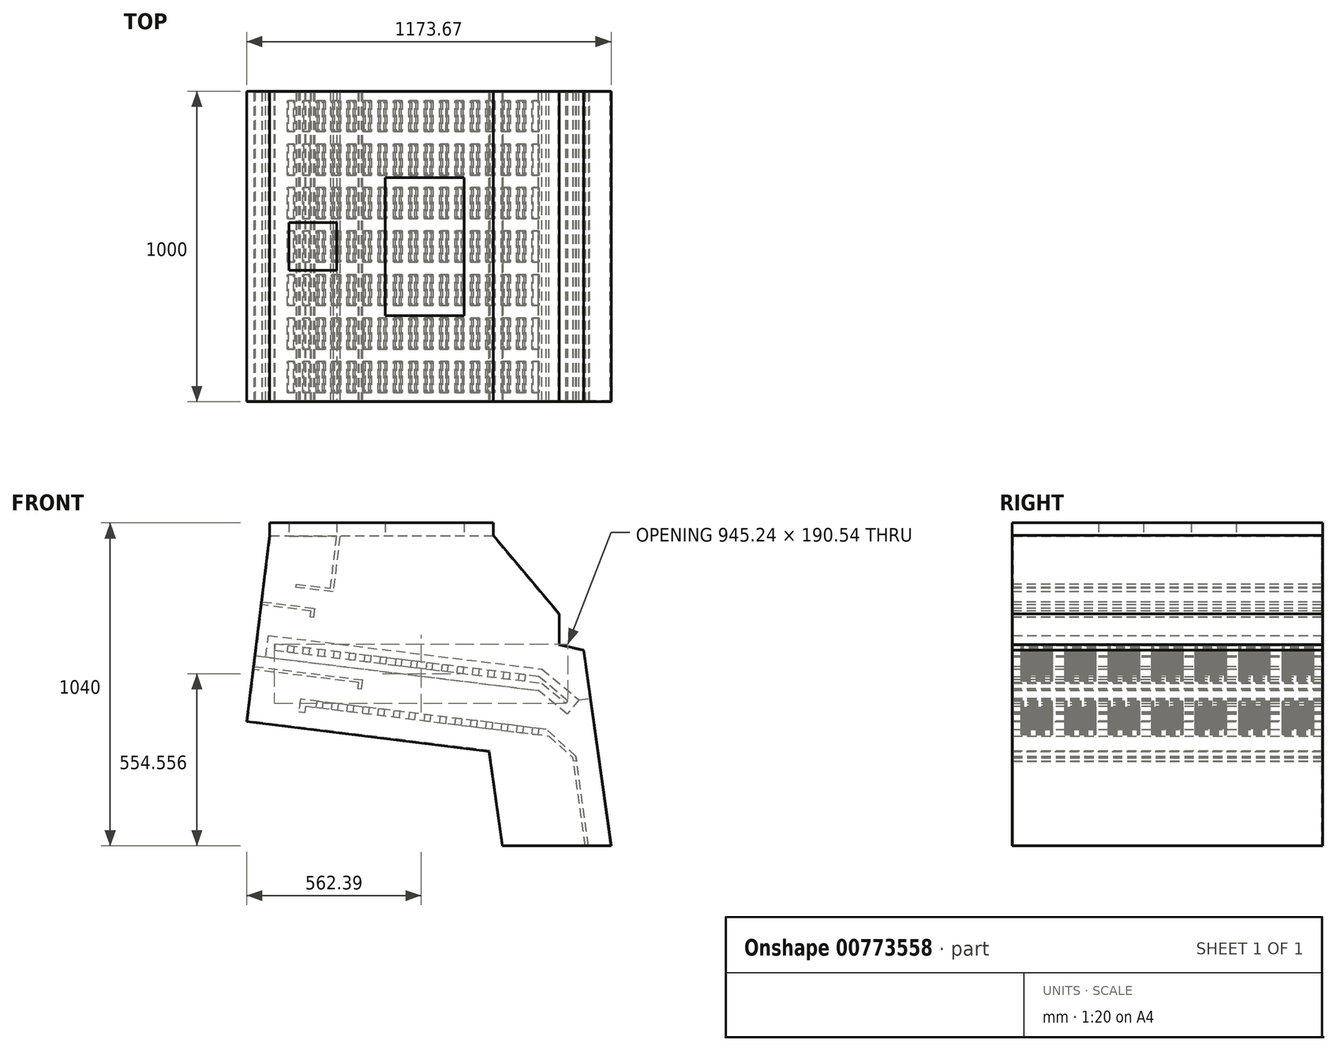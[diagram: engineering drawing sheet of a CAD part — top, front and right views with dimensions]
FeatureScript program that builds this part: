
annotation { "Feature Type Name" : "Feature", "Feature Type Description" : "" }
export const myFeature = defineFeature(function(context is Context, id is Id, definition is map)
    precondition{}
    {
        {
            var Q0;
            Q0=qCreatedBy(makeId("Front.planeOp"),FACE);
            var sketch = newSketch(context, id + "F0", { "sketchPlane" : qUnion([Q0])});
            skLineSegment(sketch, "E0.bottom", {"start": v(-500, 500) * mm, "end": v(600, 500) * mm, "construction": true});
            skLineSegment(sketch, "E0.top", {"start": v(-500, -500) * mm, "end": v(600, -500) * mm, "construction": true});
            skLineSegment(sketch, "E0.left", {"start": v(-500, 500) * mm, "end": v(-500, -500) * mm, "construction": true});
            skLineSegment(sketch, "E0.right", {"start": v(600, 500) * mm, "end": v(600, -500) * mm, "construction": true});
            skLineSegment(sketch, "E1", {"start": v(250, -500) * mm, "end": v(207.26, -195.89) * mm});
            skLineSegment(sketch, "E2", {"start": v(207.26, -195.89) * mm, "end": v(-573.67, -100) * mm});
            skLineSegment(sketch, "E3", {"start": v(433.06, 247.65) * mm, "end": v(221.32, 500) * mm});
            skLineSegment(sketch, "E4", {"start": v(221.32, 500) * mm, "end": v(-500, 500) * mm});
            skLineSegment(sketch, "E5", {"start": v(-500, 500) * mm, "end": v(-573.67, -100) * mm});
            skLineSegment(sketch, "E6", {"start": v(433.06, 247.65) * mm, "end": v(433.06, 147.65) * mm});
            skLineSegment(sketch, "E7", {"start": v(433.06, 147.65) * mm, "end": v(511.32, 131.02) * mm});
            skLineSegment(sketch, "E8", {"start": v(511.32, 131.02) * mm, "end": v(600, -500) * mm});
            skLineSegment(sketch, "E9", {"start": v(600, -500) * mm, "end": v(250, -500) * mm});
            skLineSegment(sketch, "E10", {"start": v(-573.67, -100) * mm, "end": v(788.77, -267.29) * mm, "construction": true});
            skSolve(sketch);
        }
        {
            var Q0;
            Q0 = qSketchRegion(id + "F0", true);
            extrude(context, id + "F1", {"entities" : qUnion([Q0]), "endBound" : BoundingType.SYMMETRIC, "depth" : 1000 * mm, "offsetDistance" : 25 * mm, "hasSecondDirection" : true, "secondDirectionOppositeDirection" : true, "secondDirectionDepth" : 500 * mm});
        }
        {
            var Q0;
            Q0=makeQuery(id+"F1.opExtrude","SWEPT_FACE",FACE,{"disambiguationData":[OSD([sQuery(id+"F0.wireOp",EDGE,"E4")])]});
            var sketch = newSketch(context, id + "F2", { "sketchPlane" : qUnion([Q0])});
            skLineSegment(sketch, "E11.bottom", {"start": v(-440, 80) * mm, "end": v(-280, 80) * mm});
            skLineSegment(sketch, "E11.top", {"start": v(-440, -80) * mm, "end": v(-280, -80) * mm});
            skLineSegment(sketch, "E11.left", {"start": v(-440, 80) * mm, "end": v(-440, -80) * mm});
            skLineSegment(sketch, "E11.right", {"start": v(-280, 80) * mm, "end": v(-280, -80) * mm});
            skSolve(sketch);
        }
        {
            var Q0;
            Q0 = qSketchRegion(id + "F2", true);
            extrude(context, id + "F3", {"entities" : qUnion([Q0]), "operationType" : NewBodyOperationType.ADD, "depth" : 40 * mm, "offsetDistance" : 25 * mm});
        }
        {
            var Q0;
            Q0=makeQuery(id+"F1.opExtrude","SWEPT_FACE",FACE,{"disambiguationData":[OSD([sQuery(id+"F0.wireOp",EDGE,"E4")])]});
            var sketch = newSketch(context, id + "F4", { "sketchPlane" : qUnion([Q0])});
            skLineSegment(sketch, "E12.bottom", {"start": v(130, 225) * mm, "end": v(-130, 225) * mm});
            skLineSegment(sketch, "E12.top", {"start": v(130, -225) * mm, "end": v(-130, -225) * mm});
            skLineSegment(sketch, "E12.left", {"start": v(130, 225) * mm, "end": v(130, -225) * mm});
            skLineSegment(sketch, "E12.right", {"start": v(-130, 225) * mm, "end": v(-130, -225) * mm});
            skSolve(sketch);
        }
        {
            var Q0;
            Q0 = qSketchRegion(id + "F4", true);
            extrude(context, id + "F5", {"entities" : qUnion([Q0]), "operationType" : NewBodyOperationType.ADD, "depth" : 40 * mm, "offsetDistance" : 25 * mm});
        }
        {
            var Q0;
            Q0=makeQuery(id+"F3.opExtrude","CAP_FACE",FACE,{"disambiguationData":[OSD([sQuery(id+"F2.wireOp",EDGE,"E11.bottom"),sQuery(id+"F2.wireOp",EDGE,"E11.top"),sQuery(id+"F2.wireOp",EDGE,"E11.left"),sQuery(id+"F2.wireOp",EDGE,"E11.right")])],"isStart":false});
            var Q1;
            Q1=makeQuery(id+"F5.opExtrude","CAP_FACE",FACE,{"disambiguationData":[OSD([sQuery(id+"F4.wireOp",EDGE,"E12.bottom"),sQuery(id+"F4.wireOp",EDGE,"E12.top"),sQuery(id+"F4.wireOp",EDGE,"E12.left"),sQuery(id+"F4.wireOp",EDGE,"E12.right")])],"isStart":false});
            var Q2;
            Q2=makeQuery(id+"F1.opExtrude","SWEPT_FACE",FACE,{"disambiguationData":[OSD([sQuery(id+"F0.wireOp",EDGE,"EKClBvXg-2bRz-m1K9-gZvp-cbB6sfYIkZG2")])]});
            var Q3;
            Q3=makeQuery(id+"F1.opExtrude","SWEPT_FACE",FACE,{"disambiguationData":[OSD([sQuery(id+"F0.wireOp",EDGE,"E9")])]});
            var Q4;
            Q4=makeQuery(id+"F1.opExtrude","SWEPT_BODY",BODY,{"disambiguationData":[OSD([sQuery(id+"F0.wireOp",EDGE,"E1"),sQuery(id+"F0.wireOp",EDGE,"E2"),sQuery(id+"F0.wireOp",EDGE,"E3"),sQuery(id+"F0.wireOp",EDGE,"E4"),sQuery(id+"F0.wireOp",EDGE,"E5"),sQuery(id+"F0.wireOp",EDGE,"E6"),sQuery(id+"F0.wireOp",EDGE,"E7"),sQuery(id+"F0.wireOp",EDGE,"E8"),sQuery(id+"F0.wireOp",EDGE,"xE1LlFz5-4HxX-VpLr-CkL3-rUP58BRSOtdD"),sQuery(id+"F0.wireOp",EDGE,"ObRK8uaC-pM7K-56M3-T9gG-oIo7mZDbm86T"),sQuery(id+"F0.wireOp",EDGE,"EFww76GN-BGT8-24En-PaDw-SS0GAKKsnwer"),sQuery(id+"F0.wireOp",EDGE,"E9"),sQuery(id+"F0.wireOp",EDGE,"EKClBvXg-2bRz-m1K9-gZvp-cbB6sfYIkZG2")])]});
            shell(context, id + "F6", {"entities" : qUnion([Q0, Q1, Q2, Q3]), "parts" : qUnion([Q4]), "thickness" : 3 * mm});
        }
        {
            var Q0;
            Q0=qCreatedBy(makeId("Front.planeOp"),FACE);
            var sketch = newSketch(context, id + "F7", { "sketchPlane" : qUnion([Q0])});
            skLineSegment(sketch, "E13.0", {"start": v(219.92, 497) * mm, "end": v(-497.35, 497) * mm, "construction": true});
            skLineSegment(sketch, "E14.0", {"start": v(-497.35, 497) * mm, "end": v(-570.33, -97.39) * mm, "construction": true});
            skLineSegment(sketch, "E15", {"start": v(-283, 497) * mm, "end": v(-303.57, 329.49) * mm});
            skLineSegment(sketch, "E16", {"start": v(-303.57, 329.49) * mm, "end": v(-412.75, 342.9) * mm});
            skLineSegment(sketch, "E17", {"start": v(-412.75, 342.9) * mm, "end": v(-413.97, 332.97) * mm});
            skLineSegment(sketch, "E18", {"start": v(-413.97, 332.97) * mm, "end": v(-294.86, 318.34) * mm});
            skLineSegment(sketch, "E19", {"start": v(-294.86, 318.34) * mm, "end": v(-272.92, 497) * mm});
            skLineSegment(sketch, "E20", {"start": v(-272.92, 497) * mm, "end": v(-283, 497) * mm});
            skLineSegment(sketch, "E21.0", {"start": v(-283, 540) * mm, "end": v(-283, 497) * mm, "construction": true});
            skLineSegment(sketch, "E22", {"start": v(-523.26, 285.94) * mm, "end": v(-524.48, 276) * mm});
            skLineSegment(sketch, "E23", {"start": v(-524.48, 276) * mm, "end": v(-365.67, 256.51) * mm});
            skLineSegment(sketch, "E24", {"start": v(-365.67, 256.51) * mm, "end": v(-368.11, 236.66) * mm});
            skLineSegment(sketch, "E25", {"start": v(-368.11, 236.66) * mm, "end": v(-358.18, 235.44) * mm});
            skLineSegment(sketch, "E26", {"start": v(-358.18, 235.44) * mm, "end": v(-354.53, 265.22) * mm});
            skLineSegment(sketch, "E27", {"start": v(-354.53, 265.22) * mm, "end": v(-523.26, 285.94) * mm});
            skLineSegment(sketch, "E28", {"start": v(-548.85, 77.5) * mm, "end": v(-550.07, 67.57) * mm});
            skLineSegment(sketch, "E29", {"start": v(-550.07, 67.57) * mm, "end": v(-212.6, 26.14) * mm});
            skLineSegment(sketch, "E30", {"start": v(-212.6, 26.14) * mm, "end": v(-215.04, 6.29) * mm});
            skLineSegment(sketch, "E31", {"start": v(-215.04, 6.29) * mm, "end": v(-205.12, 5.07) * mm});
            skLineSegment(sketch, "E32", {"start": v(-205.12, 5.07) * mm, "end": v(-201.46, 34.85) * mm});
            skLineSegment(sketch, "E33", {"start": v(-201.46, 34.85) * mm, "end": v(-548.85, 77.5) * mm});
            skLineSegment(sketch, "E34.0", {"start": v(209.91, -193.19) * mm, "end": v(-570.33, -97.39) * mm, "construction": true});
            skLineSegment(sketch, "E35.bottom", {"start": v(478.39, -226.15) * mm, "end": v(488.66, -227.42) * mm});
            skLineSegment(sketch, "E35.top", {"start": v(516.87, -500) * mm, "end": v(526.97, -500) * mm});
            skLineSegment(sketch, "E35.left", {"start": v(478.39, -226.15) * mm, "end": v(516.87, -500) * mm});
            skLineSegment(sketch, "E35.right", {"start": v(488.66, -227.42) * mm, "end": v(526.97, -500) * mm});
            skLineSegment(sketch, "E36", {"start": v(-570.33, -97.39) * mm, "end": v(629.89, -244.76) * mm, "construction": true});
            skLineSegment(sketch, "E37.0", {"start": v(596.97, -500) * mm, "end": v(253.03, -500) * mm, "construction": true});
            skLineSegment(sketch, "E38.0", {"start": v(508.64, 128.52) * mm, "end": v(596.97, -500) * mm, "construction": true});
            skSolve(sketch);
        }
        {
            var Q0;
            Q0 = qSketchRegion(id + "F7", true);
            var Q1;
            {var subQ0=sQuery(id+"F0.wireOp",EDGE,"E9");var subQ1=sQuery(id+"F0.wireOp",EDGE,"E8");var subQ2=sQuery(id+"F0.wireOp",EDGE,"E7");var subQ3=sQuery(id+"F0.wireOp",EDGE,"E6");var subQ4=sQuery(id+"F0.wireOp",EDGE,"E5");var subQ5=sQuery(id+"F0.wireOp",EDGE,"E4");var subQ6=sQuery(id+"F0.wireOp",EDGE,"E3");var subQ7=sQuery(id+"F0.wireOp",EDGE,"E2");var subQ8=sQuery(id+"F0.wireOp",EDGE,"E1");Q1=makeQuery(id+"F6.opShell","OFFSET_FACE",FACE,{"disambiguationData":[OSD([subQ8,subQ7,subQ6,subQ5,subQ4,subQ3,subQ2,subQ1,subQ0]),TDD([makeQuery(id+"F1.opExtrude","CAP_FACE",FACE,{"disambiguationData":[OSD([subQ8,subQ7,subQ6,subQ5,subQ4,subQ3,subQ2,subQ1,subQ0])],"isStart":true})])]});}
            var Q2;
            {var subQ0=sQuery(id+"F0.wireOp",EDGE,"E9");var subQ1=sQuery(id+"F0.wireOp",EDGE,"E8");var subQ2=sQuery(id+"F0.wireOp",EDGE,"E7");var subQ3=sQuery(id+"F0.wireOp",EDGE,"E6");var subQ4=sQuery(id+"F0.wireOp",EDGE,"E5");var subQ5=sQuery(id+"F0.wireOp",EDGE,"E4");var subQ6=sQuery(id+"F0.wireOp",EDGE,"E3");var subQ7=sQuery(id+"F0.wireOp",EDGE,"E2");var subQ8=sQuery(id+"F0.wireOp",EDGE,"E1");Q2=makeQuery(id+"F6.opShell","OFFSET_FACE",FACE,{"disambiguationData":[OSD([subQ8,subQ7,subQ6,subQ5,subQ4,subQ3,subQ2,subQ1,subQ0]),TDD([makeQuery(id+"F1.opExtrude","CAP_FACE",FACE,{"disambiguationData":[OSD([subQ8,subQ7,subQ6,subQ5,subQ4,subQ3,subQ2,subQ1,subQ0])],"isStart":false})])]});}
            extrude(context, id + "F8", {"entities" : qUnion([Q0]), "operationType" : NewBodyOperationType.ADD, "endBound" : BoundingType.UP_TO_SURFACE, "oppositeDirection" : true, "depth" : 25 * mm, "endBoundEntityFace" : qUnion([Q1]), "offsetDistance" : 25 * mm, "hasSecondDirection" : true, "secondDirectionBound" : SecondDirectionBoundingType.UP_TO_SURFACE, "secondDirectionOppositeDirection" : false, "secondDirectionDepth" : 25 * mm, "secondDirectionBoundEntityFace" : qUnion([Q2])});
        }
        {
            var Q0;
            Q0=makeQuery(id+"F1.opExtrude","SWEPT_FACE",FACE,{"disambiguationData":[OSD([sQuery(id+"F0.wireOp",EDGE,"E4")])]});
            var sketch = newSketch(context, id + "F9", { "sketchPlane" : qUnion([Q0])});
            skLineSegment(sketch, "E39.0", {"start": v(221.32, -500) * mm, "end": v(-500, -500) * mm});
            skLineSegment(sketch, "E39.1", {"start": v(-500, -500) * mm, "end": v(-500, 500) * mm});
            skLineSegment(sketch, "E39.2", {"start": v(221.32, 500) * mm, "end": v(-500, 500) * mm});
            skLineSegment(sketch, "E39.3", {"start": v(221.32, -500) * mm, "end": v(221.32, 500) * mm});
            skLineSegment(sketch, "E40.0", {"start": v(130, -225) * mm, "end": v(-130, -225) * mm});
            skLineSegment(sketch, "E40.1", {"start": v(-130, 225) * mm, "end": v(-130, -225) * mm});
            skLineSegment(sketch, "E40.2", {"start": v(130, 225) * mm, "end": v(-130, 225) * mm});
            skLineSegment(sketch, "E40.3", {"start": v(130, 225) * mm, "end": v(130, -225) * mm});
            skLineSegment(sketch, "E41.0", {"start": v(-280, 80) * mm, "end": v(-280, -80) * mm});
            skLineSegment(sketch, "E41.1", {"start": v(-440, 80) * mm, "end": v(-280, 80) * mm});
            skLineSegment(sketch, "E41.2", {"start": v(-440, 80) * mm, "end": v(-440, -80) * mm});
            skLineSegment(sketch, "E41.3", {"start": v(-440, -80) * mm, "end": v(-280, -80) * mm});
            skSolve(sketch);
        }
        {
            var Q0;
            Q0 = qSketchRegion(id + "F9", true);
            var Q1;
            Q1=makeQuery(id+"F5.opExtrude","CAP_FACE",FACE,{"disambiguationData":[OSD([sQuery(id+"F4.wireOp",EDGE,"E12.bottom"),sQuery(id+"F4.wireOp",EDGE,"E12.top"),sQuery(id+"F4.wireOp",EDGE,"E12.left"),sQuery(id+"F4.wireOp",EDGE,"E12.right")])],"isStart":false});
            extrude(context, id + "F10", {"entities" : qUnion([Q0]), "operationType" : NewBodyOperationType.ADD, "endBound" : BoundingType.UP_TO_SURFACE, "depth" : 25 * mm, "endBoundEntityFace" : qUnion([Q1]), "offsetDistance" : 25 * mm});
        }
        {
            var Q0;
            Q0=qCreatedBy(makeId("Front.planeOp"),FACE);
            var sketch = newSketch(context, id + "F11", { "sketchPlane" : qUnion([Q0])});
            skLineSegment(sketch, "E42", {"start": v(-382.59, -49.91) * mm, "end": v(399.8, -145.98) * mm});
            skLineSegment(sketch, "E43", {"start": v(399.8, -145.98) * mm, "end": v(477, -216.25) * mm});
            skLineSegment(sketch, "E44", {"start": v(486.4, -211.29) * mm, "end": v(391.4, -124.8) * mm});
            skLineSegment(sketch, "E45", {"start": v(391.4, -124.8) * mm, "end": v(-400, -27.63) * mm});
            skLineSegment(sketch, "E46", {"start": v(486.4, -211.29) * mm, "end": v(488.66, -227.42) * mm});
            skLineSegment(sketch, "E47", {"start": v(488.66, -227.42) * mm, "end": v(478.39, -226.15) * mm});
            skLineSegment(sketch, "E48", {"start": v(478.39, -226.15) * mm, "end": v(477, -216.25) * mm});
            skLineSegment(sketch, "E49", {"start": v(-400, -27.63) * mm, "end": v(-404.87, -67.33) * mm});
            skLineSegment(sketch, "E50", {"start": v(-404.87, -67.33) * mm, "end": v(-385.02, -69.76) * mm});
            skLineSegment(sketch, "E51", {"start": v(-385.02, -69.76) * mm, "end": v(-382.59, -49.91) * mm});
            skLineSegment(sketch, "E52.0", {"start": v(209.91, -193.19) * mm, "end": v(-570.33, -97.39) * mm, "construction": true});
            skLineSegment(sketch, "E53.0", {"start": v(516.87, -500) * mm, "end": v(478.39, -226.15) * mm, "construction": true});
            skLineSegment(sketch, "E53.1", {"start": v(526.97, -500) * mm, "end": v(488.66, -227.42) * mm, "construction": true});
            skLineSegment(sketch, "E53.2", {"start": v(488.66, -227.42) * mm, "end": v(478.39, -226.15) * mm, "construction": true});
            skSolve(sketch);
        }
        {
            var Q0;
            Q0 = qSketchRegion(id + "F11", true);
            var Q1;
            {var subQ0=sQuery(id+"F0.wireOp",EDGE,"E9");var subQ1=sQuery(id+"F0.wireOp",EDGE,"E8");var subQ2=sQuery(id+"F0.wireOp",EDGE,"E7");var subQ3=sQuery(id+"F0.wireOp",EDGE,"E6");var subQ4=sQuery(id+"F0.wireOp",EDGE,"E5");var subQ5=sQuery(id+"F0.wireOp",EDGE,"E4");var subQ6=sQuery(id+"F0.wireOp",EDGE,"E3");var subQ7=sQuery(id+"F0.wireOp",EDGE,"E2");var subQ8=sQuery(id+"F0.wireOp",EDGE,"E1");Q1=makeQuery(id+"F6.opShell","OFFSET_FACE",FACE,{"disambiguationData":[OSD([subQ8,subQ7,subQ6,subQ5,subQ4,subQ3,subQ2,subQ1,subQ0]),TDD([makeQuery(id+"F1.opExtrude","CAP_FACE",FACE,{"disambiguationData":[OSD([subQ8,subQ7,subQ6,subQ5,subQ4,subQ3,subQ2,subQ1,subQ0])],"isStart":false})])]});}
            var Q2;
            {var subQ0=sQuery(id+"F0.wireOp",EDGE,"E9");var subQ1=sQuery(id+"F0.wireOp",EDGE,"E8");var subQ2=sQuery(id+"F0.wireOp",EDGE,"E7");var subQ3=sQuery(id+"F0.wireOp",EDGE,"E6");var subQ4=sQuery(id+"F0.wireOp",EDGE,"E5");var subQ5=sQuery(id+"F0.wireOp",EDGE,"E4");var subQ6=sQuery(id+"F0.wireOp",EDGE,"E3");var subQ7=sQuery(id+"F0.wireOp",EDGE,"E2");var subQ8=sQuery(id+"F0.wireOp",EDGE,"E1");Q2=makeQuery(id+"F6.opShell","OFFSET_FACE",FACE,{"disambiguationData":[OSD([subQ8,subQ7,subQ6,subQ5,subQ4,subQ3,subQ2,subQ1,subQ0]),TDD([makeQuery(id+"F1.opExtrude","CAP_FACE",FACE,{"disambiguationData":[OSD([subQ8,subQ7,subQ6,subQ5,subQ4,subQ3,subQ2,subQ1,subQ0])],"isStart":true})])]});}
            extrude(context, id + "F12", {"entities" : qUnion([Q0]), "endBound" : BoundingType.UP_TO_SURFACE, "depth" : 25 * mm, "endBoundEntityFace" : qUnion([Q1]), "offsetDistance" : 25 * mm, "hasSecondDirection" : true, "secondDirectionBound" : SecondDirectionBoundingType.UP_TO_SURFACE, "secondDirectionOppositeDirection" : true, "secondDirectionDepth" : 25 * mm, "secondDirectionBoundEntityFace" : qUnion([Q2])});
        }
        {
            var Q0;
            Q0=makeQuery(id+"F12.opExtrude","SWEPT_FACE",FACE,{"disambiguationData":[OSD([sQuery(id+"F11.wireOp",EDGE,"E45")])]});
            var sketch = newSketch(context, id + "F13", { "sketchPlane" : qUnion([Q0])});
            skLineSegment(sketch, "E54", {"start": v(-605.7, 0) * mm, "end": v(761.64, 0) * mm, "construction": true});
            skLineSegment(sketch, "E55", {"start": v(0, 847.31) * mm, "end": v(0, -977.18) * mm, "construction": true});
            skLineSegment(sketch, "E56.bottom", {"start": v(380, 470) * mm, "end": v(360, 470) * mm});
            skLineSegment(sketch, "E56.top", {"start": v(380, 370) * mm, "end": v(360, 370) * mm});
            skLineSegment(sketch, "E56.left", {"start": v(380, 470) * mm, "end": v(380, 370) * mm});
            skLineSegment(sketch, "E56.right", {"start": v(360, 470) * mm, "end": v(360, 370) * mm});
            skLineSegment(sketch, "E57.0.1.0", {"start": v(380, 230) * mm, "end": v(360, 230) * mm});
            skLineSegment(sketch, "E57.0.1.1", {"start": v(380, 330) * mm, "end": v(380, 230) * mm});
            skLineSegment(sketch, "E57.0.1.2", {"start": v(360, 330) * mm, "end": v(360, 230) * mm});
            skLineSegment(sketch, "E57.0.1.3", {"start": v(380, 330) * mm, "end": v(360, 330) * mm});
            skLineSegment(sketch, "E57.0.2.0", {"start": v(380, 90) * mm, "end": v(360, 90) * mm});
            skLineSegment(sketch, "E57.0.2.1", {"start": v(380, 190) * mm, "end": v(380, 90) * mm});
            skLineSegment(sketch, "E57.0.2.2", {"start": v(360, 190) * mm, "end": v(360, 90) * mm});
            skLineSegment(sketch, "E57.0.2.3", {"start": v(380, 190) * mm, "end": v(360, 190) * mm});
            skLineSegment(sketch, "E57.0.3.0", {"start": v(380, -50) * mm, "end": v(360, -50) * mm});
            skLineSegment(sketch, "E57.0.3.1", {"start": v(380, 50) * mm, "end": v(380, -50) * mm});
            skLineSegment(sketch, "E57.0.3.2", {"start": v(360, 50) * mm, "end": v(360, -50) * mm});
            skLineSegment(sketch, "E57.0.3.3", {"start": v(380, 50) * mm, "end": v(360, 50) * mm});
            skLineSegment(sketch, "E57.0.4.0", {"start": v(380, -190) * mm, "end": v(360, -190) * mm});
            skLineSegment(sketch, "E57.0.4.1", {"start": v(380, -90) * mm, "end": v(380, -190) * mm});
            skLineSegment(sketch, "E57.0.4.2", {"start": v(360, -90) * mm, "end": v(360, -190) * mm});
            skLineSegment(sketch, "E57.0.4.3", {"start": v(380, -90) * mm, "end": v(360, -90) * mm});
            skLineSegment(sketch, "E57.0.5.0", {"start": v(380, -330) * mm, "end": v(360, -330) * mm});
            skLineSegment(sketch, "E57.0.5.1", {"start": v(380, -230) * mm, "end": v(380, -330) * mm});
            skLineSegment(sketch, "E57.0.5.2", {"start": v(360, -230) * mm, "end": v(360, -330) * mm});
            skLineSegment(sketch, "E57.0.5.3", {"start": v(380, -230) * mm, "end": v(360, -230) * mm});
            skLineSegment(sketch, "E57.0.6.0", {"start": v(380, -470) * mm, "end": v(360, -470) * mm});
            skLineSegment(sketch, "E57.0.6.1", {"start": v(380, -370) * mm, "end": v(380, -470) * mm});
            skLineSegment(sketch, "E57.0.6.2", {"start": v(360, -370) * mm, "end": v(360, -470) * mm});
            skLineSegment(sketch, "E57.0.6.3", {"start": v(380, -370) * mm, "end": v(360, -370) * mm});
            skLineSegment(sketch, "E57.1.0.0", {"start": v(330, 370) * mm, "end": v(310, 370) * mm});
            skLineSegment(sketch, "E57.1.0.1", {"start": v(330, 470) * mm, "end": v(330, 370) * mm});
            skLineSegment(sketch, "E57.1.0.2", {"start": v(310, 470) * mm, "end": v(310, 370) * mm});
            skLineSegment(sketch, "E57.1.0.3", {"start": v(330, 470) * mm, "end": v(310, 470) * mm});
            skLineSegment(sketch, "E57.1.1.0", {"start": v(330, 230) * mm, "end": v(310, 230) * mm});
            skLineSegment(sketch, "E57.1.1.1", {"start": v(330, 330) * mm, "end": v(330, 230) * mm});
            skLineSegment(sketch, "E57.1.1.2", {"start": v(310, 330) * mm, "end": v(310, 230) * mm});
            skLineSegment(sketch, "E57.1.1.3", {"start": v(330, 330) * mm, "end": v(310, 330) * mm});
            skLineSegment(sketch, "E57.1.2.0", {"start": v(330, 90) * mm, "end": v(310, 90) * mm});
            skLineSegment(sketch, "E57.1.2.1", {"start": v(330, 190) * mm, "end": v(330, 90) * mm});
            skLineSegment(sketch, "E57.1.2.2", {"start": v(310, 190) * mm, "end": v(310, 90) * mm});
            skLineSegment(sketch, "E57.1.2.3", {"start": v(330, 190) * mm, "end": v(310, 190) * mm});
            skLineSegment(sketch, "E57.1.3.0", {"start": v(330, -50) * mm, "end": v(310, -50) * mm});
            skLineSegment(sketch, "E57.1.3.1", {"start": v(330, 50) * mm, "end": v(330, -50) * mm});
            skLineSegment(sketch, "E57.1.3.2", {"start": v(310, 50) * mm, "end": v(310, -50) * mm});
            skLineSegment(sketch, "E57.1.3.3", {"start": v(330, 50) * mm, "end": v(310, 50) * mm});
            skLineSegment(sketch, "E57.1.4.0", {"start": v(330, -190) * mm, "end": v(310, -190) * mm});
            skLineSegment(sketch, "E57.1.4.1", {"start": v(330, -90) * mm, "end": v(330, -190) * mm});
            skLineSegment(sketch, "E57.1.4.2", {"start": v(310, -90) * mm, "end": v(310, -190) * mm});
            skLineSegment(sketch, "E57.1.4.3", {"start": v(330, -90) * mm, "end": v(310, -90) * mm});
            skLineSegment(sketch, "E57.1.5.0", {"start": v(330, -330) * mm, "end": v(310, -330) * mm});
            skLineSegment(sketch, "E57.1.5.1", {"start": v(330, -230) * mm, "end": v(330, -330) * mm});
            skLineSegment(sketch, "E57.1.5.2", {"start": v(310, -230) * mm, "end": v(310, -330) * mm});
            skLineSegment(sketch, "E57.1.5.3", {"start": v(330, -230) * mm, "end": v(310, -230) * mm});
            skLineSegment(sketch, "E57.1.6.0", {"start": v(330, -470) * mm, "end": v(310, -470) * mm});
            skLineSegment(sketch, "E57.1.6.1", {"start": v(330, -370) * mm, "end": v(330, -470) * mm});
            skLineSegment(sketch, "E57.1.6.2", {"start": v(310, -370) * mm, "end": v(310, -470) * mm});
            skLineSegment(sketch, "E57.1.6.3", {"start": v(330, -370) * mm, "end": v(310, -370) * mm});
            skLineSegment(sketch, "E57.2.0.0", {"start": v(280, 370) * mm, "end": v(260, 370) * mm});
            skLineSegment(sketch, "E57.2.0.1", {"start": v(280, 470) * mm, "end": v(280, 370) * mm});
            skLineSegment(sketch, "E57.2.0.2", {"start": v(260, 470) * mm, "end": v(260, 370) * mm});
            skLineSegment(sketch, "E57.2.0.3", {"start": v(280, 470) * mm, "end": v(260, 470) * mm});
            skLineSegment(sketch, "E57.2.1.0", {"start": v(280, 230) * mm, "end": v(260, 230) * mm});
            skLineSegment(sketch, "E57.2.1.1", {"start": v(280, 330) * mm, "end": v(280, 230) * mm});
            skLineSegment(sketch, "E57.2.1.2", {"start": v(260, 330) * mm, "end": v(260, 230) * mm});
            skLineSegment(sketch, "E57.2.1.3", {"start": v(280, 330) * mm, "end": v(260, 330) * mm});
            skLineSegment(sketch, "E57.2.2.0", {"start": v(280, 90) * mm, "end": v(260, 90) * mm});
            skLineSegment(sketch, "E57.2.2.1", {"start": v(280, 190) * mm, "end": v(280, 90) * mm});
            skLineSegment(sketch, "E57.2.2.2", {"start": v(260, 190) * mm, "end": v(260, 90) * mm});
            skLineSegment(sketch, "E57.2.2.3", {"start": v(280, 190) * mm, "end": v(260, 190) * mm});
            skLineSegment(sketch, "E57.2.3.0", {"start": v(280, -50) * mm, "end": v(260, -50) * mm});
            skLineSegment(sketch, "E57.2.3.1", {"start": v(280, 50) * mm, "end": v(280, -50) * mm});
            skLineSegment(sketch, "E57.2.3.2", {"start": v(260, 50) * mm, "end": v(260, -50) * mm});
            skLineSegment(sketch, "E57.2.3.3", {"start": v(280, 50) * mm, "end": v(260, 50) * mm});
            skLineSegment(sketch, "E57.2.4.0", {"start": v(280, -190) * mm, "end": v(260, -190) * mm});
            skLineSegment(sketch, "E57.2.4.1", {"start": v(280, -90) * mm, "end": v(280, -190) * mm});
            skLineSegment(sketch, "E57.2.4.2", {"start": v(260, -90) * mm, "end": v(260, -190) * mm});
            skLineSegment(sketch, "E57.2.4.3", {"start": v(280, -90) * mm, "end": v(260, -90) * mm});
            skLineSegment(sketch, "E57.2.5.0", {"start": v(280, -330) * mm, "end": v(260, -330) * mm});
            skLineSegment(sketch, "E57.2.5.1", {"start": v(280, -230) * mm, "end": v(280, -330) * mm});
            skLineSegment(sketch, "E57.2.5.2", {"start": v(260, -230) * mm, "end": v(260, -330) * mm});
            skLineSegment(sketch, "E57.2.5.3", {"start": v(280, -230) * mm, "end": v(260, -230) * mm});
            skLineSegment(sketch, "E57.2.6.0", {"start": v(280, -470) * mm, "end": v(260, -470) * mm});
            skLineSegment(sketch, "E57.2.6.1", {"start": v(280, -370) * mm, "end": v(280, -470) * mm});
            skLineSegment(sketch, "E57.2.6.2", {"start": v(260, -370) * mm, "end": v(260, -470) * mm});
            skLineSegment(sketch, "E57.2.6.3", {"start": v(280, -370) * mm, "end": v(260, -370) * mm});
            skLineSegment(sketch, "E57.direction1", {"start": v(360, 370) * mm, "end": v(310, 370) * mm, "construction": true});
            skLineSegment(sketch, "E57.direction2", {"start": v(360, 370) * mm, "end": v(360, 230) * mm, "construction": true});
            skLineSegment(sketch, "E58.0.3.0", {"start": v(230, 370) * mm, "end": v(210, 370) * mm});
            skLineSegment(sketch, "E58.3.3.0", {"start": v(230, 470) * mm, "end": v(230, 370) * mm});
            skLineSegment(sketch, "E58.6.3.0", {"start": v(210, 470) * mm, "end": v(210, 370) * mm});
            skLineSegment(sketch, "E58.9.3.0", {"start": v(230, 470) * mm, "end": v(210, 470) * mm});
            skLineSegment(sketch, "E58.0.3.1", {"start": v(230, 230) * mm, "end": v(210, 230) * mm});
            skLineSegment(sketch, "E58.3.3.1", {"start": v(230, 330) * mm, "end": v(230, 230) * mm});
            skLineSegment(sketch, "E58.6.3.1", {"start": v(210, 330) * mm, "end": v(210, 230) * mm});
            skLineSegment(sketch, "E58.9.3.1", {"start": v(230, 330) * mm, "end": v(210, 330) * mm});
            skLineSegment(sketch, "E58.0.3.2", {"start": v(230, 90) * mm, "end": v(210, 90) * mm});
            skLineSegment(sketch, "E58.3.3.2", {"start": v(230, 190) * mm, "end": v(230, 90) * mm});
            skLineSegment(sketch, "E58.6.3.2", {"start": v(210, 190) * mm, "end": v(210, 90) * mm});
            skLineSegment(sketch, "E58.9.3.2", {"start": v(230, 190) * mm, "end": v(210, 190) * mm});
            skLineSegment(sketch, "E58.0.3.3", {"start": v(230, -50) * mm, "end": v(210, -50) * mm});
            skLineSegment(sketch, "E58.3.3.3", {"start": v(230, 50) * mm, "end": v(230, -50) * mm});
            skLineSegment(sketch, "E58.6.3.3", {"start": v(210, 50) * mm, "end": v(210, -50) * mm});
            skLineSegment(sketch, "E58.9.3.3", {"start": v(230, 50) * mm, "end": v(210, 50) * mm});
            skLineSegment(sketch, "E58.0.3.4", {"start": v(230, -190) * mm, "end": v(210, -190) * mm});
            skLineSegment(sketch, "E58.3.3.4", {"start": v(230, -90) * mm, "end": v(230, -190) * mm});
            skLineSegment(sketch, "E58.6.3.4", {"start": v(210, -90) * mm, "end": v(210, -190) * mm});
            skLineSegment(sketch, "E58.9.3.4", {"start": v(230, -90) * mm, "end": v(210, -90) * mm});
            skLineSegment(sketch, "E58.0.3.5", {"start": v(230, -330) * mm, "end": v(210, -330) * mm});
            skLineSegment(sketch, "E58.3.3.5", {"start": v(230, -230) * mm, "end": v(230, -330) * mm});
            skLineSegment(sketch, "E58.6.3.5", {"start": v(210, -230) * mm, "end": v(210, -330) * mm});
            skLineSegment(sketch, "E58.9.3.5", {"start": v(230, -230) * mm, "end": v(210, -230) * mm});
            skLineSegment(sketch, "E58.0.3.6", {"start": v(230, -470) * mm, "end": v(210, -470) * mm});
            skLineSegment(sketch, "E58.3.3.6", {"start": v(230, -370) * mm, "end": v(230, -470) * mm});
            skLineSegment(sketch, "E58.6.3.6", {"start": v(210, -370) * mm, "end": v(210, -470) * mm});
            skLineSegment(sketch, "E58.9.3.6", {"start": v(230, -370) * mm, "end": v(210, -370) * mm});
            skLineSegment(sketch, "E58.0.4.0", {"start": v(180, 370) * mm, "end": v(160, 370) * mm});
            skLineSegment(sketch, "E58.3.4.0", {"start": v(180, 470) * mm, "end": v(180, 370) * mm});
            skLineSegment(sketch, "E58.6.4.0", {"start": v(160, 470) * mm, "end": v(160, 370) * mm});
            skLineSegment(sketch, "E58.9.4.0", {"start": v(180, 470) * mm, "end": v(160, 470) * mm});
            skLineSegment(sketch, "E58.0.4.1", {"start": v(180, 230) * mm, "end": v(160, 230) * mm});
            skLineSegment(sketch, "E58.3.4.1", {"start": v(180, 330) * mm, "end": v(180, 230) * mm});
            skLineSegment(sketch, "E58.6.4.1", {"start": v(160, 330) * mm, "end": v(160, 230) * mm});
            skLineSegment(sketch, "E58.9.4.1", {"start": v(180, 330) * mm, "end": v(160, 330) * mm});
            skLineSegment(sketch, "E58.0.4.2", {"start": v(180, 90) * mm, "end": v(160, 90) * mm});
            skLineSegment(sketch, "E58.3.4.2", {"start": v(180, 190) * mm, "end": v(180, 90) * mm});
            skLineSegment(sketch, "E58.6.4.2", {"start": v(160, 190) * mm, "end": v(160, 90) * mm});
            skLineSegment(sketch, "E58.9.4.2", {"start": v(180, 190) * mm, "end": v(160, 190) * mm});
            skLineSegment(sketch, "E58.0.4.3", {"start": v(180, -50) * mm, "end": v(160, -50) * mm});
            skLineSegment(sketch, "E58.3.4.3", {"start": v(180, 50) * mm, "end": v(180, -50) * mm});
            skLineSegment(sketch, "E58.6.4.3", {"start": v(160, 50) * mm, "end": v(160, -50) * mm});
            skLineSegment(sketch, "E58.9.4.3", {"start": v(180, 50) * mm, "end": v(160, 50) * mm});
            skLineSegment(sketch, "E58.0.4.4", {"start": v(180, -190) * mm, "end": v(160, -190) * mm});
            skLineSegment(sketch, "E58.3.4.4", {"start": v(180, -90) * mm, "end": v(180, -190) * mm});
            skLineSegment(sketch, "E58.6.4.4", {"start": v(160, -90) * mm, "end": v(160, -190) * mm});
            skLineSegment(sketch, "E58.9.4.4", {"start": v(180, -90) * mm, "end": v(160, -90) * mm});
            skLineSegment(sketch, "E58.0.4.5", {"start": v(180, -330) * mm, "end": v(160, -330) * mm});
            skLineSegment(sketch, "E58.3.4.5", {"start": v(180, -230) * mm, "end": v(180, -330) * mm});
            skLineSegment(sketch, "E58.6.4.5", {"start": v(160, -230) * mm, "end": v(160, -330) * mm});
            skLineSegment(sketch, "E58.9.4.5", {"start": v(180, -230) * mm, "end": v(160, -230) * mm});
            skLineSegment(sketch, "E58.0.4.6", {"start": v(180, -470) * mm, "end": v(160, -470) * mm});
            skLineSegment(sketch, "E58.3.4.6", {"start": v(180, -370) * mm, "end": v(180, -470) * mm});
            skLineSegment(sketch, "E58.6.4.6", {"start": v(160, -370) * mm, "end": v(160, -470) * mm});
            skLineSegment(sketch, "E58.9.4.6", {"start": v(180, -370) * mm, "end": v(160, -370) * mm});
            skLineSegment(sketch, "E58.0.5.0", {"start": v(130, 370) * mm, "end": v(110, 370) * mm});
            skLineSegment(sketch, "E58.3.5.0", {"start": v(130, 470) * mm, "end": v(130, 370) * mm});
            skLineSegment(sketch, "E58.6.5.0", {"start": v(110, 470) * mm, "end": v(110, 370) * mm});
            skLineSegment(sketch, "E58.9.5.0", {"start": v(130, 470) * mm, "end": v(110, 470) * mm});
            skLineSegment(sketch, "E58.0.5.1", {"start": v(130, 230) * mm, "end": v(110, 230) * mm});
            skLineSegment(sketch, "E58.3.5.1", {"start": v(130, 330) * mm, "end": v(130, 230) * mm});
            skLineSegment(sketch, "E58.6.5.1", {"start": v(110, 330) * mm, "end": v(110, 230) * mm});
            skLineSegment(sketch, "E58.9.5.1", {"start": v(130, 330) * mm, "end": v(110, 330) * mm});
            skLineSegment(sketch, "E58.0.5.2", {"start": v(130, 90) * mm, "end": v(110, 90) * mm});
            skLineSegment(sketch, "E58.3.5.2", {"start": v(130, 190) * mm, "end": v(130, 90) * mm});
            skLineSegment(sketch, "E58.6.5.2", {"start": v(110, 190) * mm, "end": v(110, 90) * mm});
            skLineSegment(sketch, "E58.9.5.2", {"start": v(130, 190) * mm, "end": v(110, 190) * mm});
            skLineSegment(sketch, "E58.0.5.3", {"start": v(130, -50) * mm, "end": v(110, -50) * mm});
            skLineSegment(sketch, "E58.3.5.3", {"start": v(130, 50) * mm, "end": v(130, -50) * mm});
            skLineSegment(sketch, "E58.6.5.3", {"start": v(110, 50) * mm, "end": v(110, -50) * mm});
            skLineSegment(sketch, "E58.9.5.3", {"start": v(130, 50) * mm, "end": v(110, 50) * mm});
            skLineSegment(sketch, "E58.0.5.4", {"start": v(130, -190) * mm, "end": v(110, -190) * mm});
            skLineSegment(sketch, "E58.3.5.4", {"start": v(130, -90) * mm, "end": v(130, -190) * mm});
            skLineSegment(sketch, "E58.6.5.4", {"start": v(110, -90) * mm, "end": v(110, -190) * mm});
            skLineSegment(sketch, "E58.9.5.4", {"start": v(130, -90) * mm, "end": v(110, -90) * mm});
            skLineSegment(sketch, "E58.0.5.5", {"start": v(130, -330) * mm, "end": v(110, -330) * mm});
            skLineSegment(sketch, "E58.3.5.5", {"start": v(130, -230) * mm, "end": v(130, -330) * mm});
            skLineSegment(sketch, "E58.6.5.5", {"start": v(110, -230) * mm, "end": v(110, -330) * mm});
            skLineSegment(sketch, "E58.9.5.5", {"start": v(130, -230) * mm, "end": v(110, -230) * mm});
            skLineSegment(sketch, "E58.0.5.6", {"start": v(130, -470) * mm, "end": v(110, -470) * mm});
            skLineSegment(sketch, "E58.3.5.6", {"start": v(130, -370) * mm, "end": v(130, -470) * mm});
            skLineSegment(sketch, "E58.6.5.6", {"start": v(110, -370) * mm, "end": v(110, -470) * mm});
            skLineSegment(sketch, "E58.9.5.6", {"start": v(130, -370) * mm, "end": v(110, -370) * mm});
            skLineSegment(sketch, "E58.0.6.0", {"start": v(80, 370) * mm, "end": v(60, 370) * mm});
            skLineSegment(sketch, "E58.3.6.0", {"start": v(80, 470) * mm, "end": v(80, 370) * mm});
            skLineSegment(sketch, "E58.6.6.0", {"start": v(60, 470) * mm, "end": v(60, 370) * mm});
            skLineSegment(sketch, "E58.9.6.0", {"start": v(80, 470) * mm, "end": v(60, 470) * mm});
            skLineSegment(sketch, "E58.0.6.1", {"start": v(80, 230) * mm, "end": v(60, 230) * mm});
            skLineSegment(sketch, "E58.3.6.1", {"start": v(80, 330) * mm, "end": v(80, 230) * mm});
            skLineSegment(sketch, "E58.6.6.1", {"start": v(60, 330) * mm, "end": v(60, 230) * mm});
            skLineSegment(sketch, "E58.9.6.1", {"start": v(80, 330) * mm, "end": v(60, 330) * mm});
            skLineSegment(sketch, "E58.0.6.2", {"start": v(80, 90) * mm, "end": v(60, 90) * mm});
            skLineSegment(sketch, "E58.3.6.2", {"start": v(80, 190) * mm, "end": v(80, 90) * mm});
            skLineSegment(sketch, "E58.6.6.2", {"start": v(60, 190) * mm, "end": v(60, 90) * mm});
            skLineSegment(sketch, "E58.9.6.2", {"start": v(80, 190) * mm, "end": v(60, 190) * mm});
            skLineSegment(sketch, "E58.0.6.3", {"start": v(80, -50) * mm, "end": v(60, -50) * mm});
            skLineSegment(sketch, "E58.3.6.3", {"start": v(80, 50) * mm, "end": v(80, -50) * mm});
            skLineSegment(sketch, "E58.6.6.3", {"start": v(60, 50) * mm, "end": v(60, -50) * mm});
            skLineSegment(sketch, "E58.9.6.3", {"start": v(80, 50) * mm, "end": v(60, 50) * mm});
            skLineSegment(sketch, "E58.0.6.4", {"start": v(80, -190) * mm, "end": v(60, -190) * mm});
            skLineSegment(sketch, "E58.3.6.4", {"start": v(80, -90) * mm, "end": v(80, -190) * mm});
            skLineSegment(sketch, "E58.6.6.4", {"start": v(60, -90) * mm, "end": v(60, -190) * mm});
            skLineSegment(sketch, "E58.9.6.4", {"start": v(80, -90) * mm, "end": v(60, -90) * mm});
            skLineSegment(sketch, "E58.0.6.5", {"start": v(80, -330) * mm, "end": v(60, -330) * mm});
            skLineSegment(sketch, "E58.3.6.5", {"start": v(80, -230) * mm, "end": v(80, -330) * mm});
            skLineSegment(sketch, "E58.6.6.5", {"start": v(60, -230) * mm, "end": v(60, -330) * mm});
            skLineSegment(sketch, "E58.9.6.5", {"start": v(80, -230) * mm, "end": v(60, -230) * mm});
            skLineSegment(sketch, "E58.0.6.6", {"start": v(80, -470) * mm, "end": v(60, -470) * mm});
            skLineSegment(sketch, "E58.3.6.6", {"start": v(80, -370) * mm, "end": v(80, -470) * mm});
            skLineSegment(sketch, "E58.6.6.6", {"start": v(60, -370) * mm, "end": v(60, -470) * mm});
            skLineSegment(sketch, "E58.9.6.6", {"start": v(80, -370) * mm, "end": v(60, -370) * mm});
            skLineSegment(sketch, "E58.0.7.0", {"start": v(30, 370) * mm, "end": v(10, 370) * mm});
            skLineSegment(sketch, "E58.3.7.0", {"start": v(30, 470) * mm, "end": v(30, 370) * mm});
            skLineSegment(sketch, "E58.6.7.0", {"start": v(10, 470) * mm, "end": v(10, 370) * mm});
            skLineSegment(sketch, "E58.9.7.0", {"start": v(30, 470) * mm, "end": v(10, 470) * mm});
            skLineSegment(sketch, "E58.0.7.1", {"start": v(30, 230) * mm, "end": v(10, 230) * mm});
            skLineSegment(sketch, "E58.3.7.1", {"start": v(30, 330) * mm, "end": v(30, 230) * mm});
            skLineSegment(sketch, "E58.6.7.1", {"start": v(10, 330) * mm, "end": v(10, 230) * mm});
            skLineSegment(sketch, "E58.9.7.1", {"start": v(30, 330) * mm, "end": v(10, 330) * mm});
            skLineSegment(sketch, "E58.0.7.2", {"start": v(30, 90) * mm, "end": v(10, 90) * mm});
            skLineSegment(sketch, "E58.3.7.2", {"start": v(30, 190) * mm, "end": v(30, 90) * mm});
            skLineSegment(sketch, "E58.6.7.2", {"start": v(10, 190) * mm, "end": v(10, 90) * mm});
            skLineSegment(sketch, "E58.9.7.2", {"start": v(30, 190) * mm, "end": v(10, 190) * mm});
            skLineSegment(sketch, "E58.0.7.3", {"start": v(30, -50) * mm, "end": v(10, -50) * mm});
            skLineSegment(sketch, "E58.3.7.3", {"start": v(30, 50) * mm, "end": v(30, -50) * mm});
            skLineSegment(sketch, "E58.6.7.3", {"start": v(10, 50) * mm, "end": v(10, -50) * mm});
            skLineSegment(sketch, "E58.9.7.3", {"start": v(30, 50) * mm, "end": v(10, 50) * mm});
            skLineSegment(sketch, "E58.0.7.4", {"start": v(30, -190) * mm, "end": v(10, -190) * mm});
            skLineSegment(sketch, "E58.3.7.4", {"start": v(30, -90) * mm, "end": v(30, -190) * mm});
            skLineSegment(sketch, "E58.6.7.4", {"start": v(10, -90) * mm, "end": v(10, -190) * mm});
            skLineSegment(sketch, "E58.9.7.4", {"start": v(30, -90) * mm, "end": v(10, -90) * mm});
            skLineSegment(sketch, "E58.0.7.5", {"start": v(30, -330) * mm, "end": v(10, -330) * mm});
            skLineSegment(sketch, "E58.3.7.5", {"start": v(30, -230) * mm, "end": v(30, -330) * mm});
            skLineSegment(sketch, "E58.6.7.5", {"start": v(10, -230) * mm, "end": v(10, -330) * mm});
            skLineSegment(sketch, "E58.9.7.5", {"start": v(30, -230) * mm, "end": v(10, -230) * mm});
            skLineSegment(sketch, "E58.0.7.6", {"start": v(30, -470) * mm, "end": v(10, -470) * mm});
            skLineSegment(sketch, "E58.3.7.6", {"start": v(30, -370) * mm, "end": v(30, -470) * mm});
            skLineSegment(sketch, "E58.6.7.6", {"start": v(10, -370) * mm, "end": v(10, -470) * mm});
            skLineSegment(sketch, "E58.9.7.6", {"start": v(30, -370) * mm, "end": v(10, -370) * mm});
            skLineSegment(sketch, "E58.0.8.0", {"start": v(-20, 370) * mm, "end": v(-40, 370) * mm});
            skLineSegment(sketch, "E58.3.8.0", {"start": v(-20, 470) * mm, "end": v(-20, 370) * mm});
            skLineSegment(sketch, "E58.6.8.0", {"start": v(-40, 470) * mm, "end": v(-40, 370) * mm});
            skLineSegment(sketch, "E58.9.8.0", {"start": v(-20, 470) * mm, "end": v(-40, 470) * mm});
            skLineSegment(sketch, "E58.0.8.1", {"start": v(-20, 230) * mm, "end": v(-40, 230) * mm});
            skLineSegment(sketch, "E58.3.8.1", {"start": v(-20, 330) * mm, "end": v(-20, 230) * mm});
            skLineSegment(sketch, "E58.6.8.1", {"start": v(-40, 330) * mm, "end": v(-40, 230) * mm});
            skLineSegment(sketch, "E58.9.8.1", {"start": v(-20, 330) * mm, "end": v(-40, 330) * mm});
            skLineSegment(sketch, "E58.0.8.2", {"start": v(-20, 90) * mm, "end": v(-40, 90) * mm});
            skLineSegment(sketch, "E58.3.8.2", {"start": v(-20, 190) * mm, "end": v(-20, 90) * mm});
            skLineSegment(sketch, "E58.6.8.2", {"start": v(-40, 190) * mm, "end": v(-40, 90) * mm});
            skLineSegment(sketch, "E58.9.8.2", {"start": v(-20, 190) * mm, "end": v(-40, 190) * mm});
            skLineSegment(sketch, "E58.0.8.3", {"start": v(-20, -50) * mm, "end": v(-40, -50) * mm});
            skLineSegment(sketch, "E58.3.8.3", {"start": v(-20, 50) * mm, "end": v(-20, -50) * mm});
            skLineSegment(sketch, "E58.6.8.3", {"start": v(-40, 50) * mm, "end": v(-40, -50) * mm});
            skLineSegment(sketch, "E58.9.8.3", {"start": v(-20, 50) * mm, "end": v(-40, 50) * mm});
            skLineSegment(sketch, "E58.0.8.4", {"start": v(-20, -190) * mm, "end": v(-40, -190) * mm});
            skLineSegment(sketch, "E58.3.8.4", {"start": v(-20, -90) * mm, "end": v(-20, -190) * mm});
            skLineSegment(sketch, "E58.6.8.4", {"start": v(-40, -90) * mm, "end": v(-40, -190) * mm});
            skLineSegment(sketch, "E58.9.8.4", {"start": v(-20, -90) * mm, "end": v(-40, -90) * mm});
            skLineSegment(sketch, "E58.0.8.5", {"start": v(-20, -330) * mm, "end": v(-40, -330) * mm});
            skLineSegment(sketch, "E58.3.8.5", {"start": v(-20, -230) * mm, "end": v(-20, -330) * mm});
            skLineSegment(sketch, "E58.6.8.5", {"start": v(-40, -230) * mm, "end": v(-40, -330) * mm});
            skLineSegment(sketch, "E58.9.8.5", {"start": v(-20, -230) * mm, "end": v(-40, -230) * mm});
            skLineSegment(sketch, "E58.0.8.6", {"start": v(-20, -470) * mm, "end": v(-40, -470) * mm});
            skLineSegment(sketch, "E58.3.8.6", {"start": v(-20, -370) * mm, "end": v(-20, -470) * mm});
            skLineSegment(sketch, "E58.6.8.6", {"start": v(-40, -370) * mm, "end": v(-40, -470) * mm});
            skLineSegment(sketch, "E58.9.8.6", {"start": v(-20, -370) * mm, "end": v(-40, -370) * mm});
            skLineSegment(sketch, "E58.0.9.0", {"start": v(-70, 370) * mm, "end": v(-90, 370) * mm});
            skLineSegment(sketch, "E58.3.9.0", {"start": v(-70, 470) * mm, "end": v(-70, 370) * mm});
            skLineSegment(sketch, "E58.6.9.0", {"start": v(-90, 470) * mm, "end": v(-90, 370) * mm});
            skLineSegment(sketch, "E58.9.9.0", {"start": v(-70, 470) * mm, "end": v(-90, 470) * mm});
            skLineSegment(sketch, "E58.0.9.1", {"start": v(-70, 230) * mm, "end": v(-90, 230) * mm});
            skLineSegment(sketch, "E58.3.9.1", {"start": v(-70, 330) * mm, "end": v(-70, 230) * mm});
            skLineSegment(sketch, "E58.6.9.1", {"start": v(-90, 330) * mm, "end": v(-90, 230) * mm});
            skLineSegment(sketch, "E58.9.9.1", {"start": v(-70, 330) * mm, "end": v(-90, 330) * mm});
            skLineSegment(sketch, "E58.0.9.2", {"start": v(-70, 90) * mm, "end": v(-90, 90) * mm});
            skLineSegment(sketch, "E58.3.9.2", {"start": v(-70, 190) * mm, "end": v(-70, 90) * mm});
            skLineSegment(sketch, "E58.6.9.2", {"start": v(-90, 190) * mm, "end": v(-90, 90) * mm});
            skLineSegment(sketch, "E58.9.9.2", {"start": v(-70, 190) * mm, "end": v(-90, 190) * mm});
            skLineSegment(sketch, "E58.0.9.3", {"start": v(-70, -50) * mm, "end": v(-90, -50) * mm});
            skLineSegment(sketch, "E58.3.9.3", {"start": v(-70, 50) * mm, "end": v(-70, -50) * mm});
            skLineSegment(sketch, "E58.6.9.3", {"start": v(-90, 50) * mm, "end": v(-90, -50) * mm});
            skLineSegment(sketch, "E58.9.9.3", {"start": v(-70, 50) * mm, "end": v(-90, 50) * mm});
            skLineSegment(sketch, "E58.0.9.4", {"start": v(-70, -190) * mm, "end": v(-90, -190) * mm});
            skLineSegment(sketch, "E58.3.9.4", {"start": v(-70, -90) * mm, "end": v(-70, -190) * mm});
            skLineSegment(sketch, "E58.6.9.4", {"start": v(-90, -90) * mm, "end": v(-90, -190) * mm});
            skLineSegment(sketch, "E58.9.9.4", {"start": v(-70, -90) * mm, "end": v(-90, -90) * mm});
            skLineSegment(sketch, "E58.0.9.5", {"start": v(-70, -330) * mm, "end": v(-90, -330) * mm});
            skLineSegment(sketch, "E58.3.9.5", {"start": v(-70, -230) * mm, "end": v(-70, -330) * mm});
            skLineSegment(sketch, "E58.6.9.5", {"start": v(-90, -230) * mm, "end": v(-90, -330) * mm});
            skLineSegment(sketch, "E58.9.9.5", {"start": v(-70, -230) * mm, "end": v(-90, -230) * mm});
            skLineSegment(sketch, "E58.0.9.6", {"start": v(-70, -470) * mm, "end": v(-90, -470) * mm});
            skLineSegment(sketch, "E58.3.9.6", {"start": v(-70, -370) * mm, "end": v(-70, -470) * mm});
            skLineSegment(sketch, "E58.6.9.6", {"start": v(-90, -370) * mm, "end": v(-90, -470) * mm});
            skLineSegment(sketch, "E58.9.9.6", {"start": v(-70, -370) * mm, "end": v(-90, -370) * mm});
            skLineSegment(sketch, "E58.0.10.0", {"start": v(-120, 370) * mm, "end": v(-140, 370) * mm});
            skLineSegment(sketch, "E58.3.10.0", {"start": v(-120, 470) * mm, "end": v(-120, 370) * mm});
            skLineSegment(sketch, "E58.6.10.0", {"start": v(-140, 470) * mm, "end": v(-140, 370) * mm});
            skLineSegment(sketch, "E58.9.10.0", {"start": v(-120, 470) * mm, "end": v(-140, 470) * mm});
            skLineSegment(sketch, "E58.0.10.1", {"start": v(-120, 230) * mm, "end": v(-140, 230) * mm});
            skLineSegment(sketch, "E58.3.10.1", {"start": v(-120, 330) * mm, "end": v(-120, 230) * mm});
            skLineSegment(sketch, "E58.6.10.1", {"start": v(-140, 330) * mm, "end": v(-140, 230) * mm});
            skLineSegment(sketch, "E58.9.10.1", {"start": v(-120, 330) * mm, "end": v(-140, 330) * mm});
            skLineSegment(sketch, "E58.0.10.2", {"start": v(-120, 90) * mm, "end": v(-140, 90) * mm});
            skLineSegment(sketch, "E58.3.10.2", {"start": v(-120, 190) * mm, "end": v(-120, 90) * mm});
            skLineSegment(sketch, "E58.6.10.2", {"start": v(-140, 190) * mm, "end": v(-140, 90) * mm});
            skLineSegment(sketch, "E58.9.10.2", {"start": v(-120, 190) * mm, "end": v(-140, 190) * mm});
            skLineSegment(sketch, "E58.0.10.3", {"start": v(-120, -50) * mm, "end": v(-140, -50) * mm});
            skLineSegment(sketch, "E58.3.10.3", {"start": v(-120, 50) * mm, "end": v(-120, -50) * mm});
            skLineSegment(sketch, "E58.6.10.3", {"start": v(-140, 50) * mm, "end": v(-140, -50) * mm});
            skLineSegment(sketch, "E58.9.10.3", {"start": v(-120, 50) * mm, "end": v(-140, 50) * mm});
            skLineSegment(sketch, "E58.0.10.4", {"start": v(-120, -190) * mm, "end": v(-140, -190) * mm});
            skLineSegment(sketch, "E58.3.10.4", {"start": v(-120, -90) * mm, "end": v(-120, -190) * mm});
            skLineSegment(sketch, "E58.6.10.4", {"start": v(-140, -90) * mm, "end": v(-140, -190) * mm});
            skLineSegment(sketch, "E58.9.10.4", {"start": v(-120, -90) * mm, "end": v(-140, -90) * mm});
            skLineSegment(sketch, "E58.0.10.5", {"start": v(-120, -330) * mm, "end": v(-140, -330) * mm});
            skLineSegment(sketch, "E58.3.10.5", {"start": v(-120, -230) * mm, "end": v(-120, -330) * mm});
            skLineSegment(sketch, "E58.6.10.5", {"start": v(-140, -230) * mm, "end": v(-140, -330) * mm});
            skLineSegment(sketch, "E58.9.10.5", {"start": v(-120, -230) * mm, "end": v(-140, -230) * mm});
            skLineSegment(sketch, "E58.0.10.6", {"start": v(-120, -470) * mm, "end": v(-140, -470) * mm});
            skLineSegment(sketch, "E58.3.10.6", {"start": v(-120, -370) * mm, "end": v(-120, -470) * mm});
            skLineSegment(sketch, "E58.6.10.6", {"start": v(-140, -370) * mm, "end": v(-140, -470) * mm});
            skLineSegment(sketch, "E58.9.10.6", {"start": v(-120, -370) * mm, "end": v(-140, -370) * mm});
            skLineSegment(sketch, "E58.0.11.0", {"start": v(-170, 370) * mm, "end": v(-190, 370) * mm});
            skLineSegment(sketch, "E58.3.11.0", {"start": v(-170, 470) * mm, "end": v(-170, 370) * mm});
            skLineSegment(sketch, "E58.6.11.0", {"start": v(-190, 470) * mm, "end": v(-190, 370) * mm});
            skLineSegment(sketch, "E58.9.11.0", {"start": v(-170, 470) * mm, "end": v(-190, 470) * mm});
            skLineSegment(sketch, "E58.0.11.1", {"start": v(-170, 230) * mm, "end": v(-190, 230) * mm});
            skLineSegment(sketch, "E58.3.11.1", {"start": v(-170, 330) * mm, "end": v(-170, 230) * mm});
            skLineSegment(sketch, "E58.6.11.1", {"start": v(-190, 330) * mm, "end": v(-190, 230) * mm});
            skLineSegment(sketch, "E58.9.11.1", {"start": v(-170, 330) * mm, "end": v(-190, 330) * mm});
            skLineSegment(sketch, "E58.0.11.2", {"start": v(-170, 90) * mm, "end": v(-190, 90) * mm});
            skLineSegment(sketch, "E58.3.11.2", {"start": v(-170, 190) * mm, "end": v(-170, 90) * mm});
            skLineSegment(sketch, "E58.6.11.2", {"start": v(-190, 190) * mm, "end": v(-190, 90) * mm});
            skLineSegment(sketch, "E58.9.11.2", {"start": v(-170, 190) * mm, "end": v(-190, 190) * mm});
            skLineSegment(sketch, "E58.0.11.3", {"start": v(-170, -50) * mm, "end": v(-190, -50) * mm});
            skLineSegment(sketch, "E58.3.11.3", {"start": v(-170, 50) * mm, "end": v(-170, -50) * mm});
            skLineSegment(sketch, "E58.6.11.3", {"start": v(-190, 50) * mm, "end": v(-190, -50) * mm});
            skLineSegment(sketch, "E58.9.11.3", {"start": v(-170, 50) * mm, "end": v(-190, 50) * mm});
            skLineSegment(sketch, "E58.0.11.4", {"start": v(-170, -190) * mm, "end": v(-190, -190) * mm});
            skLineSegment(sketch, "E58.3.11.4", {"start": v(-170, -90) * mm, "end": v(-170, -190) * mm});
            skLineSegment(sketch, "E58.6.11.4", {"start": v(-190, -90) * mm, "end": v(-190, -190) * mm});
            skLineSegment(sketch, "E58.9.11.4", {"start": v(-170, -90) * mm, "end": v(-190, -90) * mm});
            skLineSegment(sketch, "E58.0.11.5", {"start": v(-170, -330) * mm, "end": v(-190, -330) * mm});
            skLineSegment(sketch, "E58.3.11.5", {"start": v(-170, -230) * mm, "end": v(-170, -330) * mm});
            skLineSegment(sketch, "E58.6.11.5", {"start": v(-190, -230) * mm, "end": v(-190, -330) * mm});
            skLineSegment(sketch, "E58.9.11.5", {"start": v(-170, -230) * mm, "end": v(-190, -230) * mm});
            skLineSegment(sketch, "E58.0.11.6", {"start": v(-170, -470) * mm, "end": v(-190, -470) * mm});
            skLineSegment(sketch, "E58.3.11.6", {"start": v(-170, -370) * mm, "end": v(-170, -470) * mm});
            skLineSegment(sketch, "E58.6.11.6", {"start": v(-190, -370) * mm, "end": v(-190, -470) * mm});
            skLineSegment(sketch, "E58.9.11.6", {"start": v(-170, -370) * mm, "end": v(-190, -370) * mm});
            skLineSegment(sketch, "E58.0.12.0", {"start": v(-220, 370) * mm, "end": v(-240, 370) * mm});
            skLineSegment(sketch, "E58.3.12.0", {"start": v(-220, 470) * mm, "end": v(-220, 370) * mm});
            skLineSegment(sketch, "E58.6.12.0", {"start": v(-240, 470) * mm, "end": v(-240, 370) * mm});
            skLineSegment(sketch, "E58.9.12.0", {"start": v(-220, 470) * mm, "end": v(-240, 470) * mm});
            skLineSegment(sketch, "E58.0.12.1", {"start": v(-220, 230) * mm, "end": v(-240, 230) * mm});
            skLineSegment(sketch, "E58.3.12.1", {"start": v(-220, 330) * mm, "end": v(-220, 230) * mm});
            skLineSegment(sketch, "E58.6.12.1", {"start": v(-240, 330) * mm, "end": v(-240, 230) * mm});
            skLineSegment(sketch, "E58.9.12.1", {"start": v(-220, 330) * mm, "end": v(-240, 330) * mm});
            skLineSegment(sketch, "E58.0.12.2", {"start": v(-220, 90) * mm, "end": v(-240, 90) * mm});
            skLineSegment(sketch, "E58.3.12.2", {"start": v(-220, 190) * mm, "end": v(-220, 90) * mm});
            skLineSegment(sketch, "E58.6.12.2", {"start": v(-240, 190) * mm, "end": v(-240, 90) * mm});
            skLineSegment(sketch, "E58.9.12.2", {"start": v(-220, 190) * mm, "end": v(-240, 190) * mm});
            skLineSegment(sketch, "E58.0.12.3", {"start": v(-220, -50) * mm, "end": v(-240, -50) * mm});
            skLineSegment(sketch, "E58.3.12.3", {"start": v(-220, 50) * mm, "end": v(-220, -50) * mm});
            skLineSegment(sketch, "E58.6.12.3", {"start": v(-240, 50) * mm, "end": v(-240, -50) * mm});
            skLineSegment(sketch, "E58.9.12.3", {"start": v(-220, 50) * mm, "end": v(-240, 50) * mm});
            skLineSegment(sketch, "E58.0.12.4", {"start": v(-220, -190) * mm, "end": v(-240, -190) * mm});
            skLineSegment(sketch, "E58.3.12.4", {"start": v(-220, -90) * mm, "end": v(-220, -190) * mm});
            skLineSegment(sketch, "E58.6.12.4", {"start": v(-240, -90) * mm, "end": v(-240, -190) * mm});
            skLineSegment(sketch, "E58.9.12.4", {"start": v(-220, -90) * mm, "end": v(-240, -90) * mm});
            skLineSegment(sketch, "E58.0.12.5", {"start": v(-220, -330) * mm, "end": v(-240, -330) * mm});
            skLineSegment(sketch, "E58.3.12.5", {"start": v(-220, -230) * mm, "end": v(-220, -330) * mm});
            skLineSegment(sketch, "E58.6.12.5", {"start": v(-240, -230) * mm, "end": v(-240, -330) * mm});
            skLineSegment(sketch, "E58.9.12.5", {"start": v(-220, -230) * mm, "end": v(-240, -230) * mm});
            skLineSegment(sketch, "E58.0.12.6", {"start": v(-220, -470) * mm, "end": v(-240, -470) * mm});
            skLineSegment(sketch, "E58.3.12.6", {"start": v(-220, -370) * mm, "end": v(-220, -470) * mm});
            skLineSegment(sketch, "E58.6.12.6", {"start": v(-240, -370) * mm, "end": v(-240, -470) * mm});
            skLineSegment(sketch, "E58.9.12.6", {"start": v(-220, -370) * mm, "end": v(-240, -370) * mm});
            skLineSegment(sketch, "E58.0.13.0", {"start": v(-270, 370) * mm, "end": v(-290, 370) * mm});
            skLineSegment(sketch, "E58.3.13.0", {"start": v(-270, 470) * mm, "end": v(-270, 370) * mm});
            skLineSegment(sketch, "E58.6.13.0", {"start": v(-290, 470) * mm, "end": v(-290, 370) * mm});
            skLineSegment(sketch, "E58.9.13.0", {"start": v(-270, 470) * mm, "end": v(-290, 470) * mm});
            skLineSegment(sketch, "E58.0.13.1", {"start": v(-270, 230) * mm, "end": v(-290, 230) * mm});
            skLineSegment(sketch, "E58.3.13.1", {"start": v(-270, 330) * mm, "end": v(-270, 230) * mm});
            skLineSegment(sketch, "E58.6.13.1", {"start": v(-290, 330) * mm, "end": v(-290, 230) * mm});
            skLineSegment(sketch, "E58.9.13.1", {"start": v(-270, 330) * mm, "end": v(-290, 330) * mm});
            skLineSegment(sketch, "E58.0.13.2", {"start": v(-270, 90) * mm, "end": v(-290, 90) * mm});
            skLineSegment(sketch, "E58.3.13.2", {"start": v(-270, 190) * mm, "end": v(-270, 90) * mm});
            skLineSegment(sketch, "E58.6.13.2", {"start": v(-290, 190) * mm, "end": v(-290, 90) * mm});
            skLineSegment(sketch, "E58.9.13.2", {"start": v(-270, 190) * mm, "end": v(-290, 190) * mm});
            skLineSegment(sketch, "E58.0.13.3", {"start": v(-270, -50) * mm, "end": v(-290, -50) * mm});
            skLineSegment(sketch, "E58.3.13.3", {"start": v(-270, 50) * mm, "end": v(-270, -50) * mm});
            skLineSegment(sketch, "E58.6.13.3", {"start": v(-290, 50) * mm, "end": v(-290, -50) * mm});
            skLineSegment(sketch, "E58.9.13.3", {"start": v(-270, 50) * mm, "end": v(-290, 50) * mm});
            skLineSegment(sketch, "E58.0.13.4", {"start": v(-270, -190) * mm, "end": v(-290, -190) * mm});
            skLineSegment(sketch, "E58.3.13.4", {"start": v(-270, -90) * mm, "end": v(-270, -190) * mm});
            skLineSegment(sketch, "E58.6.13.4", {"start": v(-290, -90) * mm, "end": v(-290, -190) * mm});
            skLineSegment(sketch, "E58.9.13.4", {"start": v(-270, -90) * mm, "end": v(-290, -90) * mm});
            skLineSegment(sketch, "E58.0.13.5", {"start": v(-270, -330) * mm, "end": v(-290, -330) * mm});
            skLineSegment(sketch, "E58.3.13.5", {"start": v(-270, -230) * mm, "end": v(-270, -330) * mm});
            skLineSegment(sketch, "E58.6.13.5", {"start": v(-290, -230) * mm, "end": v(-290, -330) * mm});
            skLineSegment(sketch, "E58.9.13.5", {"start": v(-270, -230) * mm, "end": v(-290, -230) * mm});
            skLineSegment(sketch, "E58.0.13.6", {"start": v(-270, -470) * mm, "end": v(-290, -470) * mm});
            skLineSegment(sketch, "E58.3.13.6", {"start": v(-270, -370) * mm, "end": v(-270, -470) * mm});
            skLineSegment(sketch, "E58.6.13.6", {"start": v(-290, -370) * mm, "end": v(-290, -470) * mm});
            skLineSegment(sketch, "E58.9.13.6", {"start": v(-270, -370) * mm, "end": v(-290, -370) * mm});
            skLineSegment(sketch, "E58.0.14.0", {"start": v(-320, 370) * mm, "end": v(-340, 370) * mm});
            skLineSegment(sketch, "E58.3.14.0", {"start": v(-320, 470) * mm, "end": v(-320, 370) * mm});
            skLineSegment(sketch, "E58.6.14.0", {"start": v(-340, 470) * mm, "end": v(-340, 370) * mm});
            skLineSegment(sketch, "E58.9.14.0", {"start": v(-320, 470) * mm, "end": v(-340, 470) * mm});
            skLineSegment(sketch, "E58.0.14.1", {"start": v(-320, 230) * mm, "end": v(-340, 230) * mm});
            skLineSegment(sketch, "E58.3.14.1", {"start": v(-320, 330) * mm, "end": v(-320, 230) * mm});
            skLineSegment(sketch, "E58.6.14.1", {"start": v(-340, 330) * mm, "end": v(-340, 230) * mm});
            skLineSegment(sketch, "E58.9.14.1", {"start": v(-320, 330) * mm, "end": v(-340, 330) * mm});
            skLineSegment(sketch, "E58.0.14.2", {"start": v(-320, 90) * mm, "end": v(-340, 90) * mm});
            skLineSegment(sketch, "E58.3.14.2", {"start": v(-320, 190) * mm, "end": v(-320, 90) * mm});
            skLineSegment(sketch, "E58.6.14.2", {"start": v(-340, 190) * mm, "end": v(-340, 90) * mm});
            skLineSegment(sketch, "E58.9.14.2", {"start": v(-320, 190) * mm, "end": v(-340, 190) * mm});
            skLineSegment(sketch, "E58.0.14.3", {"start": v(-320, -50) * mm, "end": v(-340, -50) * mm});
            skLineSegment(sketch, "E58.3.14.3", {"start": v(-320, 50) * mm, "end": v(-320, -50) * mm});
            skLineSegment(sketch, "E58.6.14.3", {"start": v(-340, 50) * mm, "end": v(-340, -50) * mm});
            skLineSegment(sketch, "E58.9.14.3", {"start": v(-320, 50) * mm, "end": v(-340, 50) * mm});
            skLineSegment(sketch, "E58.0.14.4", {"start": v(-320, -190) * mm, "end": v(-340, -190) * mm});
            skLineSegment(sketch, "E58.3.14.4", {"start": v(-320, -90) * mm, "end": v(-320, -190) * mm});
            skLineSegment(sketch, "E58.6.14.4", {"start": v(-340, -90) * mm, "end": v(-340, -190) * mm});
            skLineSegment(sketch, "E58.9.14.4", {"start": v(-320, -90) * mm, "end": v(-340, -90) * mm});
            skLineSegment(sketch, "E58.0.14.5", {"start": v(-320, -330) * mm, "end": v(-340, -330) * mm});
            skLineSegment(sketch, "E58.3.14.5", {"start": v(-320, -230) * mm, "end": v(-320, -330) * mm});
            skLineSegment(sketch, "E58.6.14.5", {"start": v(-340, -230) * mm, "end": v(-340, -330) * mm});
            skLineSegment(sketch, "E58.9.14.5", {"start": v(-320, -230) * mm, "end": v(-340, -230) * mm});
            skLineSegment(sketch, "E58.0.14.6", {"start": v(-320, -470) * mm, "end": v(-340, -470) * mm});
            skLineSegment(sketch, "E58.3.14.6", {"start": v(-320, -370) * mm, "end": v(-320, -470) * mm});
            skLineSegment(sketch, "E58.6.14.6", {"start": v(-340, -370) * mm, "end": v(-340, -470) * mm});
            skLineSegment(sketch, "E58.9.14.6", {"start": v(-320, -370) * mm, "end": v(-340, -370) * mm});
            skSolve(sketch);
        }
        {
            var Q0;
            Q0 = qSketchRegion(id + "F13", true);
            var Q1;
            Q1=makeQuery(id+"F12.opExtrude","SWEPT_FACE",FACE,{"disambiguationData":[OSD([sQuery(id+"F11.wireOp",EDGE,"E42")])]});
            extrude(context, id + "F14", {"entities" : qUnion([Q0]), "operationType" : NewBodyOperationType.REMOVE, "endBound" : BoundingType.UP_TO_SURFACE, "oppositeDirection" : true, "depth" : 25 * mm, "endBoundEntityFace" : qUnion([Q1]), "offsetDistance" : 25 * mm});
        }
        {
            var Q0;
            Q0=qCreatedBy(makeId("Front.planeOp"),FACE);
            var sketch = newSketch(context, id + "F15", { "sketchPlane" : qUnion([Q0])});
            skLineSegment(sketch, "E59", {"start": v(-481.46, 149.83) * mm, "end": v(666.43, 8.88) * mm, "construction": true});
            skLineSegment(sketch, "E60.0", {"start": v(-548.85, 77.5) * mm, "end": v(-201.46, 34.85) * mm, "construction": true});
            skLineSegment(sketch, "E61", {"start": v(-483.9, 129.98) * mm, "end": v(376.48, 24.33) * mm});
            skLineSegment(sketch, "E62", {"start": v(376.48, 24.33) * mm, "end": v(454.96, -40.71) * mm});
            skLineSegment(sketch, "E63", {"start": v(461.34, -33.02) * mm, "end": v(366.34, 45.73) * mm});
            skLineSegment(sketch, "E64", {"start": v(366.34, 45.73) * mm, "end": v(-481.46, 149.83) * mm});
            skLineSegment(sketch, "E65", {"start": v(-481.46, 149.83) * mm, "end": v(-483.9, 129.98) * mm});
            skLineSegment(sketch, "E66.1", {"start": v(500.94, -314.76) * mm, "end": v(461.34, -33.02) * mm, "construction": true});
            skLineSegment(sketch, "E67", {"start": v(454.96, -40.71) * mm, "end": v(461.34, -33.02) * mm});
            skSolve(sketch);
        }
        {
            var Q0;
            Q0 = qSketchRegion(id + "F15", true);
            var Q1;
            {var subQ0=sQuery(id+"F0.wireOp",EDGE,"E9");var subQ1=sQuery(id+"F0.wireOp",EDGE,"E8");var subQ2=sQuery(id+"F0.wireOp",EDGE,"E7");var subQ3=sQuery(id+"F0.wireOp",EDGE,"E6");var subQ4=sQuery(id+"F0.wireOp",EDGE,"E5");var subQ5=sQuery(id+"F0.wireOp",EDGE,"E4");var subQ6=sQuery(id+"F0.wireOp",EDGE,"E3");var subQ7=sQuery(id+"F0.wireOp",EDGE,"E2");var subQ8=sQuery(id+"F0.wireOp",EDGE,"E1");Q1=makeQuery(id+"F6.opShell","OFFSET_FACE",FACE,{"disambiguationData":[OSD([subQ8,subQ7,subQ6,subQ5,subQ4,subQ3,subQ2,subQ1,subQ0]),TDD([makeQuery(id+"F1.opExtrude","CAP_FACE",FACE,{"disambiguationData":[OSD([subQ8,subQ7,subQ6,subQ5,subQ4,subQ3,subQ2,subQ1,subQ0])],"isStart":false})])]});}
            var Q2;
            {var subQ0=sQuery(id+"F0.wireOp",EDGE,"E9");var subQ1=sQuery(id+"F0.wireOp",EDGE,"E8");var subQ2=sQuery(id+"F0.wireOp",EDGE,"E7");var subQ3=sQuery(id+"F0.wireOp",EDGE,"E6");var subQ4=sQuery(id+"F0.wireOp",EDGE,"E5");var subQ5=sQuery(id+"F0.wireOp",EDGE,"E4");var subQ6=sQuery(id+"F0.wireOp",EDGE,"E3");var subQ7=sQuery(id+"F0.wireOp",EDGE,"E2");var subQ8=sQuery(id+"F0.wireOp",EDGE,"E1");Q2=makeQuery(id+"F6.opShell","OFFSET_FACE",FACE,{"disambiguationData":[OSD([subQ8,subQ7,subQ6,subQ5,subQ4,subQ3,subQ2,subQ1,subQ0]),TDD([makeQuery(id+"F1.opExtrude","CAP_FACE",FACE,{"disambiguationData":[OSD([subQ8,subQ7,subQ6,subQ5,subQ4,subQ3,subQ2,subQ1,subQ0])],"isStart":true})])]});}
            extrude(context, id + "F16", {"entities" : qUnion([Q0]), "endBound" : BoundingType.UP_TO_SURFACE, "depth" : 25 * mm, "endBoundEntityFace" : qUnion([Q1]), "offsetDistance" : 25 * mm, "hasSecondDirection" : true, "secondDirectionBound" : SecondDirectionBoundingType.UP_TO_SURFACE, "secondDirectionOppositeDirection" : true, "secondDirectionDepth" : 25 * mm, "secondDirectionBoundEntityFace" : qUnion([Q2])});
        }
        {
            var Q0;
            Q0=makeQuery(id+"F16.opExtrude","SWEPT_FACE",FACE,{"disambiguationData":[OSD([sQuery(id+"F15.wireOp",EDGE,"E64")])]});
            var sketch = newSketch(context, id + "F17", { "sketchPlane" : qUnion([Q0])});
            skLineSegment(sketch, "E68", {"start": v(542.68, 0) * mm, "end": v(-642.45, 0) * mm, "construction": true});
            skPoint(sketch, "E68.startSnap0", {"position": v(358.04, 0) * mm});
            skLineSegment(sketch, "E69", {"start": v(-69.05, 735.3) * mm, "end": v(-69.05, -918.6) * mm, "construction": true});
            skPoint(sketch, "E69.startSnap0", {"position": v(-69.05, 497) * mm});
            skLineSegment(sketch, "E70", {"start": v(-674.76, 0) * mm, "end": v(692.6, 0) * mm, "construction": true});
            skLineSegment(sketch, "E71", {"start": v(-69.05, 847.31) * mm, "end": v(-69.05, -977.18) * mm, "construction": true});
            skLineSegment(sketch, "E72.bottom", {"start": v(315.95, 470) * mm, "end": v(295.95, 470) * mm});
            skLineSegment(sketch, "E72.top", {"start": v(315.95, 370) * mm, "end": v(295.95, 370) * mm});
            skLineSegment(sketch, "E72.left", {"start": v(315.95, 470) * mm, "end": v(315.95, 370) * mm});
            skLineSegment(sketch, "E72.right", {"start": v(295.95, 470) * mm, "end": v(295.95, 370) * mm});
            skLineSegment(sketch, "E73.0.1.0", {"start": v(315.95, 230) * mm, "end": v(295.95, 230) * mm});
            skLineSegment(sketch, "E73.0.1.1", {"start": v(315.95, 330) * mm, "end": v(315.95, 230) * mm});
            skLineSegment(sketch, "E73.0.1.2", {"start": v(295.95, 330) * mm, "end": v(295.95, 230) * mm});
            skLineSegment(sketch, "E73.0.1.3", {"start": v(315.95, 330) * mm, "end": v(295.95, 330) * mm});
            skLineSegment(sketch, "E73.0.2.0", {"start": v(315.95, 90) * mm, "end": v(295.95, 90) * mm});
            skLineSegment(sketch, "E73.0.2.1", {"start": v(315.95, 190) * mm, "end": v(315.95, 90) * mm});
            skLineSegment(sketch, "E73.0.2.2", {"start": v(295.95, 190) * mm, "end": v(295.95, 90) * mm});
            skLineSegment(sketch, "E73.0.2.3", {"start": v(315.95, 190) * mm, "end": v(295.95, 190) * mm});
            skLineSegment(sketch, "E73.0.3.0", {"start": v(315.95, -50) * mm, "end": v(295.95, -50) * mm});
            skLineSegment(sketch, "E73.0.3.1", {"start": v(315.95, 50) * mm, "end": v(315.95, -50) * mm});
            skLineSegment(sketch, "E73.0.3.2", {"start": v(295.95, 50) * mm, "end": v(295.95, -50) * mm});
            skLineSegment(sketch, "E73.0.3.3", {"start": v(315.95, 50) * mm, "end": v(295.95, 50) * mm});
            skLineSegment(sketch, "E73.0.4.0", {"start": v(315.95, -190) * mm, "end": v(295.95, -190) * mm});
            skLineSegment(sketch, "E73.0.4.1", {"start": v(315.95, -90) * mm, "end": v(315.95, -190) * mm});
            skLineSegment(sketch, "E73.0.4.2", {"start": v(295.95, -90) * mm, "end": v(295.95, -190) * mm});
            skLineSegment(sketch, "E73.0.4.3", {"start": v(315.95, -90) * mm, "end": v(295.95, -90) * mm});
            skLineSegment(sketch, "E73.0.5.0", {"start": v(315.95, -330) * mm, "end": v(295.95, -330) * mm});
            skLineSegment(sketch, "E73.0.5.1", {"start": v(315.95, -230) * mm, "end": v(315.95, -330) * mm});
            skLineSegment(sketch, "E73.0.5.2", {"start": v(295.95, -230) * mm, "end": v(295.95, -330) * mm});
            skLineSegment(sketch, "E73.0.5.3", {"start": v(315.95, -230) * mm, "end": v(295.95, -230) * mm});
            skLineSegment(sketch, "E73.0.6.0", {"start": v(315.95, -470) * mm, "end": v(295.95, -470) * mm});
            skLineSegment(sketch, "E73.0.6.1", {"start": v(315.95, -370) * mm, "end": v(315.95, -470) * mm});
            skLineSegment(sketch, "E73.0.6.2", {"start": v(295.95, -370) * mm, "end": v(295.95, -470) * mm});
            skLineSegment(sketch, "E73.0.6.3", {"start": v(315.95, -370) * mm, "end": v(295.95, -370) * mm});
            skLineSegment(sketch, "E73.1.0.0", {"start": v(265.95, 370) * mm, "end": v(245.95, 370) * mm});
            skLineSegment(sketch, "E73.1.0.1", {"start": v(265.95, 470) * mm, "end": v(265.95, 370) * mm});
            skLineSegment(sketch, "E73.1.0.2", {"start": v(245.95, 470) * mm, "end": v(245.95, 370) * mm});
            skLineSegment(sketch, "E73.1.0.3", {"start": v(265.95, 470) * mm, "end": v(245.95, 470) * mm});
            skLineSegment(sketch, "E73.1.1.0", {"start": v(265.95, 230) * mm, "end": v(245.95, 230) * mm});
            skLineSegment(sketch, "E73.1.1.1", {"start": v(265.95, 330) * mm, "end": v(265.95, 230) * mm});
            skLineSegment(sketch, "E73.1.1.2", {"start": v(245.95, 330) * mm, "end": v(245.95, 230) * mm});
            skLineSegment(sketch, "E73.1.1.3", {"start": v(265.95, 330) * mm, "end": v(245.95, 330) * mm});
            skLineSegment(sketch, "E73.1.2.0", {"start": v(265.95, 90) * mm, "end": v(245.95, 90) * mm});
            skLineSegment(sketch, "E73.1.2.1", {"start": v(265.95, 190) * mm, "end": v(265.95, 90) * mm});
            skLineSegment(sketch, "E73.1.2.2", {"start": v(245.95, 190) * mm, "end": v(245.95, 90) * mm});
            skLineSegment(sketch, "E73.1.2.3", {"start": v(265.95, 190) * mm, "end": v(245.95, 190) * mm});
            skLineSegment(sketch, "E73.1.3.0", {"start": v(265.95, -50) * mm, "end": v(245.95, -50) * mm});
            skLineSegment(sketch, "E73.1.3.1", {"start": v(265.95, 50) * mm, "end": v(265.95, -50) * mm});
            skLineSegment(sketch, "E73.1.3.2", {"start": v(245.95, 50) * mm, "end": v(245.95, -50) * mm});
            skLineSegment(sketch, "E73.1.3.3", {"start": v(265.95, 50) * mm, "end": v(245.95, 50) * mm});
            skLineSegment(sketch, "E73.1.4.0", {"start": v(265.95, -190) * mm, "end": v(245.95, -190) * mm});
            skLineSegment(sketch, "E73.1.4.1", {"start": v(265.95, -90) * mm, "end": v(265.95, -190) * mm});
            skLineSegment(sketch, "E73.1.4.2", {"start": v(245.95, -90) * mm, "end": v(245.95, -190) * mm});
            skLineSegment(sketch, "E73.1.4.3", {"start": v(265.95, -90) * mm, "end": v(245.95, -90) * mm});
            skLineSegment(sketch, "E73.1.5.0", {"start": v(265.95, -330) * mm, "end": v(245.95, -330) * mm});
            skLineSegment(sketch, "E73.1.5.1", {"start": v(265.95, -230) * mm, "end": v(265.95, -330) * mm});
            skLineSegment(sketch, "E73.1.5.2", {"start": v(245.95, -230) * mm, "end": v(245.95, -330) * mm});
            skLineSegment(sketch, "E73.1.5.3", {"start": v(265.95, -230) * mm, "end": v(245.95, -230) * mm});
            skLineSegment(sketch, "E73.1.6.0", {"start": v(265.95, -470) * mm, "end": v(245.95, -470) * mm});
            skLineSegment(sketch, "E73.1.6.1", {"start": v(265.95, -370) * mm, "end": v(265.95, -470) * mm});
            skLineSegment(sketch, "E73.1.6.2", {"start": v(245.95, -370) * mm, "end": v(245.95, -470) * mm});
            skLineSegment(sketch, "E73.1.6.3", {"start": v(265.95, -370) * mm, "end": v(245.95, -370) * mm});
            skLineSegment(sketch, "E73.2.0.0", {"start": v(215.95, 370) * mm, "end": v(195.95, 370) * mm});
            skLineSegment(sketch, "E73.2.0.1", {"start": v(215.95, 470) * mm, "end": v(215.95, 370) * mm});
            skLineSegment(sketch, "E73.2.0.2", {"start": v(195.95, 470) * mm, "end": v(195.95, 370) * mm});
            skLineSegment(sketch, "E73.2.0.3", {"start": v(215.95, 470) * mm, "end": v(195.95, 470) * mm});
            skLineSegment(sketch, "E73.2.1.0", {"start": v(215.95, 230) * mm, "end": v(195.95, 230) * mm});
            skLineSegment(sketch, "E73.2.1.1", {"start": v(215.95, 330) * mm, "end": v(215.95, 230) * mm});
            skLineSegment(sketch, "E73.2.1.2", {"start": v(195.95, 330) * mm, "end": v(195.95, 230) * mm});
            skLineSegment(sketch, "E73.2.1.3", {"start": v(215.95, 330) * mm, "end": v(195.95, 330) * mm});
            skLineSegment(sketch, "E73.2.2.0", {"start": v(215.95, 90) * mm, "end": v(195.95, 90) * mm});
            skLineSegment(sketch, "E73.2.2.1", {"start": v(215.95, 190) * mm, "end": v(215.95, 90) * mm});
            skLineSegment(sketch, "E73.2.2.2", {"start": v(195.95, 190) * mm, "end": v(195.95, 90) * mm});
            skLineSegment(sketch, "E73.2.2.3", {"start": v(215.95, 190) * mm, "end": v(195.95, 190) * mm});
            skLineSegment(sketch, "E73.2.3.0", {"start": v(215.95, -50) * mm, "end": v(195.95, -50) * mm});
            skLineSegment(sketch, "E73.2.3.1", {"start": v(215.95, 50) * mm, "end": v(215.95, -50) * mm});
            skLineSegment(sketch, "E73.2.3.2", {"start": v(195.95, 50) * mm, "end": v(195.95, -50) * mm});
            skLineSegment(sketch, "E73.2.3.3", {"start": v(215.95, 50) * mm, "end": v(195.95, 50) * mm});
            skLineSegment(sketch, "E73.2.4.0", {"start": v(215.95, -190) * mm, "end": v(195.95, -190) * mm});
            skLineSegment(sketch, "E73.2.4.1", {"start": v(215.95, -90) * mm, "end": v(215.95, -190) * mm});
            skLineSegment(sketch, "E73.2.4.2", {"start": v(195.95, -90) * mm, "end": v(195.95, -190) * mm});
            skLineSegment(sketch, "E73.2.4.3", {"start": v(215.95, -90) * mm, "end": v(195.95, -90) * mm});
            skLineSegment(sketch, "E73.2.5.0", {"start": v(215.95, -330) * mm, "end": v(195.95, -330) * mm});
            skLineSegment(sketch, "E73.2.5.1", {"start": v(215.95, -230) * mm, "end": v(215.95, -330) * mm});
            skLineSegment(sketch, "E73.2.5.2", {"start": v(195.95, -230) * mm, "end": v(195.95, -330) * mm});
            skLineSegment(sketch, "E73.2.5.3", {"start": v(215.95, -230) * mm, "end": v(195.95, -230) * mm});
            skLineSegment(sketch, "E73.2.6.0", {"start": v(215.95, -470) * mm, "end": v(195.95, -470) * mm});
            skLineSegment(sketch, "E73.2.6.1", {"start": v(215.95, -370) * mm, "end": v(215.95, -470) * mm});
            skLineSegment(sketch, "E73.2.6.2", {"start": v(195.95, -370) * mm, "end": v(195.95, -470) * mm});
            skLineSegment(sketch, "E73.2.6.3", {"start": v(215.95, -370) * mm, "end": v(195.95, -370) * mm});
            skLineSegment(sketch, "E73.direction1", {"start": v(295.95, 370) * mm, "end": v(245.95, 370) * mm, "construction": true});
            skLineSegment(sketch, "E73.direction2", {"start": v(295.95, 370) * mm, "end": v(295.95, 230) * mm, "construction": true});
            skLineSegment(sketch, "E74.0.3.0", {"start": v(165.95, 370) * mm, "end": v(145.95, 370) * mm});
            skLineSegment(sketch, "E74.3.3.0", {"start": v(165.95, 470) * mm, "end": v(165.95, 370) * mm});
            skLineSegment(sketch, "E74.6.3.0", {"start": v(145.95, 470) * mm, "end": v(145.95, 370) * mm});
            skLineSegment(sketch, "E74.9.3.0", {"start": v(165.95, 470) * mm, "end": v(145.95, 470) * mm});
            skLineSegment(sketch, "E74.0.3.1", {"start": v(165.95, 230) * mm, "end": v(145.95, 230) * mm});
            skLineSegment(sketch, "E74.3.3.1", {"start": v(165.95, 330) * mm, "end": v(165.95, 230) * mm});
            skLineSegment(sketch, "E74.6.3.1", {"start": v(145.95, 330) * mm, "end": v(145.95, 230) * mm});
            skLineSegment(sketch, "E74.9.3.1", {"start": v(165.95, 330) * mm, "end": v(145.95, 330) * mm});
            skLineSegment(sketch, "E74.0.3.2", {"start": v(165.95, 90) * mm, "end": v(145.95, 90) * mm});
            skLineSegment(sketch, "E74.3.3.2", {"start": v(165.95, 190) * mm, "end": v(165.95, 90) * mm});
            skLineSegment(sketch, "E74.6.3.2", {"start": v(145.95, 190) * mm, "end": v(145.95, 90) * mm});
            skLineSegment(sketch, "E74.9.3.2", {"start": v(165.95, 190) * mm, "end": v(145.95, 190) * mm});
            skLineSegment(sketch, "E74.0.3.3", {"start": v(165.95, -50) * mm, "end": v(145.95, -50) * mm});
            skLineSegment(sketch, "E74.3.3.3", {"start": v(165.95, 50) * mm, "end": v(165.95, -50) * mm});
            skLineSegment(sketch, "E74.6.3.3", {"start": v(145.95, 50) * mm, "end": v(145.95, -50) * mm});
            skLineSegment(sketch, "E74.9.3.3", {"start": v(165.95, 50) * mm, "end": v(145.95, 50) * mm});
            skLineSegment(sketch, "E74.0.3.4", {"start": v(165.95, -190) * mm, "end": v(145.95, -190) * mm});
            skLineSegment(sketch, "E74.3.3.4", {"start": v(165.95, -90) * mm, "end": v(165.95, -190) * mm});
            skLineSegment(sketch, "E74.6.3.4", {"start": v(145.95, -90) * mm, "end": v(145.95, -190) * mm});
            skLineSegment(sketch, "E74.9.3.4", {"start": v(165.95, -90) * mm, "end": v(145.95, -90) * mm});
            skLineSegment(sketch, "E74.0.3.5", {"start": v(165.95, -330) * mm, "end": v(145.95, -330) * mm});
            skLineSegment(sketch, "E74.3.3.5", {"start": v(165.95, -230) * mm, "end": v(165.95, -330) * mm});
            skLineSegment(sketch, "E74.6.3.5", {"start": v(145.95, -230) * mm, "end": v(145.95, -330) * mm});
            skLineSegment(sketch, "E74.9.3.5", {"start": v(165.95, -230) * mm, "end": v(145.95, -230) * mm});
            skLineSegment(sketch, "E74.0.3.6", {"start": v(165.95, -470) * mm, "end": v(145.95, -470) * mm});
            skLineSegment(sketch, "E74.3.3.6", {"start": v(165.95, -370) * mm, "end": v(165.95, -470) * mm});
            skLineSegment(sketch, "E74.6.3.6", {"start": v(145.95, -370) * mm, "end": v(145.95, -470) * mm});
            skLineSegment(sketch, "E74.9.3.6", {"start": v(165.95, -370) * mm, "end": v(145.95, -370) * mm});
            skLineSegment(sketch, "E74.0.4.0", {"start": v(115.95, 370) * mm, "end": v(95.95, 370) * mm});
            skLineSegment(sketch, "E74.3.4.0", {"start": v(115.95, 470) * mm, "end": v(115.95, 370) * mm});
            skLineSegment(sketch, "E74.6.4.0", {"start": v(95.95, 470) * mm, "end": v(95.95, 370) * mm});
            skLineSegment(sketch, "E74.9.4.0", {"start": v(115.95, 470) * mm, "end": v(95.95, 470) * mm});
            skLineSegment(sketch, "E74.0.4.1", {"start": v(115.95, 230) * mm, "end": v(95.95, 230) * mm});
            skLineSegment(sketch, "E74.3.4.1", {"start": v(115.95, 330) * mm, "end": v(115.95, 230) * mm});
            skLineSegment(sketch, "E74.6.4.1", {"start": v(95.95, 330) * mm, "end": v(95.95, 230) * mm});
            skLineSegment(sketch, "E74.9.4.1", {"start": v(115.95, 330) * mm, "end": v(95.95, 330) * mm});
            skLineSegment(sketch, "E74.0.4.2", {"start": v(115.95, 90) * mm, "end": v(95.95, 90) * mm});
            skLineSegment(sketch, "E74.3.4.2", {"start": v(115.95, 190) * mm, "end": v(115.95, 90) * mm});
            skLineSegment(sketch, "E74.6.4.2", {"start": v(95.95, 190) * mm, "end": v(95.95, 90) * mm});
            skLineSegment(sketch, "E74.9.4.2", {"start": v(115.95, 190) * mm, "end": v(95.95, 190) * mm});
            skLineSegment(sketch, "E74.0.4.3", {"start": v(115.95, -50) * mm, "end": v(95.95, -50) * mm});
            skLineSegment(sketch, "E74.3.4.3", {"start": v(115.95, 50) * mm, "end": v(115.95, -50) * mm});
            skLineSegment(sketch, "E74.6.4.3", {"start": v(95.95, 50) * mm, "end": v(95.95, -50) * mm});
            skLineSegment(sketch, "E74.9.4.3", {"start": v(115.95, 50) * mm, "end": v(95.95, 50) * mm});
            skLineSegment(sketch, "E74.0.4.4", {"start": v(115.95, -190) * mm, "end": v(95.95, -190) * mm});
            skLineSegment(sketch, "E74.3.4.4", {"start": v(115.95, -90) * mm, "end": v(115.95, -190) * mm});
            skLineSegment(sketch, "E74.6.4.4", {"start": v(95.95, -90) * mm, "end": v(95.95, -190) * mm});
            skLineSegment(sketch, "E74.9.4.4", {"start": v(115.95, -90) * mm, "end": v(95.95, -90) * mm});
            skLineSegment(sketch, "E74.0.4.5", {"start": v(115.95, -330) * mm, "end": v(95.95, -330) * mm});
            skLineSegment(sketch, "E74.3.4.5", {"start": v(115.95, -230) * mm, "end": v(115.95, -330) * mm});
            skLineSegment(sketch, "E74.6.4.5", {"start": v(95.95, -230) * mm, "end": v(95.95, -330) * mm});
            skLineSegment(sketch, "E74.9.4.5", {"start": v(115.95, -230) * mm, "end": v(95.95, -230) * mm});
            skLineSegment(sketch, "E74.0.4.6", {"start": v(115.95, -470) * mm, "end": v(95.95, -470) * mm});
            skLineSegment(sketch, "E74.3.4.6", {"start": v(115.95, -370) * mm, "end": v(115.95, -470) * mm});
            skLineSegment(sketch, "E74.6.4.6", {"start": v(95.95, -370) * mm, "end": v(95.95, -470) * mm});
            skLineSegment(sketch, "E74.9.4.6", {"start": v(115.95, -370) * mm, "end": v(95.95, -370) * mm});
            skLineSegment(sketch, "E74.0.5.0", {"start": v(65.95, 370) * mm, "end": v(45.95, 370) * mm});
            skLineSegment(sketch, "E74.3.5.0", {"start": v(65.95, 470) * mm, "end": v(65.95, 370) * mm});
            skLineSegment(sketch, "E74.6.5.0", {"start": v(45.95, 470) * mm, "end": v(45.95, 370) * mm});
            skLineSegment(sketch, "E74.9.5.0", {"start": v(65.95, 470) * mm, "end": v(45.95, 470) * mm});
            skLineSegment(sketch, "E74.0.5.1", {"start": v(65.95, 230) * mm, "end": v(45.95, 230) * mm});
            skLineSegment(sketch, "E74.3.5.1", {"start": v(65.95, 330) * mm, "end": v(65.95, 230) * mm});
            skLineSegment(sketch, "E74.6.5.1", {"start": v(45.95, 330) * mm, "end": v(45.95, 230) * mm});
            skLineSegment(sketch, "E74.9.5.1", {"start": v(65.95, 330) * mm, "end": v(45.95, 330) * mm});
            skLineSegment(sketch, "E74.0.5.2", {"start": v(65.95, 90) * mm, "end": v(45.95, 90) * mm});
            skLineSegment(sketch, "E74.3.5.2", {"start": v(65.95, 190) * mm, "end": v(65.95, 90) * mm});
            skLineSegment(sketch, "E74.6.5.2", {"start": v(45.95, 190) * mm, "end": v(45.95, 90) * mm});
            skLineSegment(sketch, "E74.9.5.2", {"start": v(65.95, 190) * mm, "end": v(45.95, 190) * mm});
            skLineSegment(sketch, "E74.0.5.3", {"start": v(65.95, -50) * mm, "end": v(45.95, -50) * mm});
            skLineSegment(sketch, "E74.3.5.3", {"start": v(65.95, 50) * mm, "end": v(65.95, -50) * mm});
            skLineSegment(sketch, "E74.6.5.3", {"start": v(45.95, 50) * mm, "end": v(45.95, -50) * mm});
            skLineSegment(sketch, "E74.9.5.3", {"start": v(65.95, 50) * mm, "end": v(45.95, 50) * mm});
            skLineSegment(sketch, "E74.0.5.4", {"start": v(65.95, -190) * mm, "end": v(45.95, -190) * mm});
            skLineSegment(sketch, "E74.3.5.4", {"start": v(65.95, -90) * mm, "end": v(65.95, -190) * mm});
            skLineSegment(sketch, "E74.6.5.4", {"start": v(45.95, -90) * mm, "end": v(45.95, -190) * mm});
            skLineSegment(sketch, "E74.9.5.4", {"start": v(65.95, -90) * mm, "end": v(45.95, -90) * mm});
            skLineSegment(sketch, "E74.0.5.5", {"start": v(65.95, -330) * mm, "end": v(45.95, -330) * mm});
            skLineSegment(sketch, "E74.3.5.5", {"start": v(65.95, -230) * mm, "end": v(65.95, -330) * mm});
            skLineSegment(sketch, "E74.6.5.5", {"start": v(45.95, -230) * mm, "end": v(45.95, -330) * mm});
            skLineSegment(sketch, "E74.9.5.5", {"start": v(65.95, -230) * mm, "end": v(45.95, -230) * mm});
            skLineSegment(sketch, "E74.0.5.6", {"start": v(65.95, -470) * mm, "end": v(45.95, -470) * mm});
            skLineSegment(sketch, "E74.3.5.6", {"start": v(65.95, -370) * mm, "end": v(65.95, -470) * mm});
            skLineSegment(sketch, "E74.6.5.6", {"start": v(45.95, -370) * mm, "end": v(45.95, -470) * mm});
            skLineSegment(sketch, "E74.9.5.6", {"start": v(65.95, -370) * mm, "end": v(45.95, -370) * mm});
            skLineSegment(sketch, "E74.0.6.0", {"start": v(15.95, 370) * mm, "end": v(-4.05, 370) * mm});
            skLineSegment(sketch, "E74.3.6.0", {"start": v(15.95, 470) * mm, "end": v(15.95, 370) * mm});
            skLineSegment(sketch, "E74.6.6.0", {"start": v(-4.05, 470) * mm, "end": v(-4.05, 370) * mm});
            skLineSegment(sketch, "E74.9.6.0", {"start": v(15.95, 470) * mm, "end": v(-4.05, 470) * mm});
            skLineSegment(sketch, "E74.0.6.1", {"start": v(15.95, 230) * mm, "end": v(-4.05, 230) * mm});
            skLineSegment(sketch, "E74.3.6.1", {"start": v(15.95, 330) * mm, "end": v(15.95, 230) * mm});
            skLineSegment(sketch, "E74.6.6.1", {"start": v(-4.05, 330) * mm, "end": v(-4.05, 230) * mm});
            skLineSegment(sketch, "E74.9.6.1", {"start": v(15.95, 330) * mm, "end": v(-4.05, 330) * mm});
            skLineSegment(sketch, "E74.0.6.2", {"start": v(15.95, 90) * mm, "end": v(-4.05, 90) * mm});
            skLineSegment(sketch, "E74.3.6.2", {"start": v(15.95, 190) * mm, "end": v(15.95, 90) * mm});
            skLineSegment(sketch, "E74.6.6.2", {"start": v(-4.05, 190) * mm, "end": v(-4.05, 90) * mm});
            skLineSegment(sketch, "E74.9.6.2", {"start": v(15.95, 190) * mm, "end": v(-4.05, 190) * mm});
            skLineSegment(sketch, "E74.0.6.3", {"start": v(15.95, -50) * mm, "end": v(-4.05, -50) * mm});
            skLineSegment(sketch, "E74.3.6.3", {"start": v(15.95, 50) * mm, "end": v(15.95, -50) * mm});
            skLineSegment(sketch, "E74.6.6.3", {"start": v(-4.05, 50) * mm, "end": v(-4.05, -50) * mm});
            skLineSegment(sketch, "E74.9.6.3", {"start": v(15.95, 50) * mm, "end": v(-4.05, 50) * mm});
            skLineSegment(sketch, "E74.0.6.4", {"start": v(15.95, -190) * mm, "end": v(-4.05, -190) * mm});
            skLineSegment(sketch, "E74.3.6.4", {"start": v(15.95, -90) * mm, "end": v(15.95, -190) * mm});
            skLineSegment(sketch, "E74.6.6.4", {"start": v(-4.05, -90) * mm, "end": v(-4.05, -190) * mm});
            skLineSegment(sketch, "E74.9.6.4", {"start": v(15.95, -90) * mm, "end": v(-4.05, -90) * mm});
            skLineSegment(sketch, "E74.0.6.5", {"start": v(15.95, -330) * mm, "end": v(-4.05, -330) * mm});
            skLineSegment(sketch, "E74.3.6.5", {"start": v(15.95, -230) * mm, "end": v(15.95, -330) * mm});
            skLineSegment(sketch, "E74.6.6.5", {"start": v(-4.05, -230) * mm, "end": v(-4.05, -330) * mm});
            skLineSegment(sketch, "E74.9.6.5", {"start": v(15.95, -230) * mm, "end": v(-4.05, -230) * mm});
            skLineSegment(sketch, "E74.0.6.6", {"start": v(15.95, -470) * mm, "end": v(-4.05, -470) * mm});
            skLineSegment(sketch, "E74.3.6.6", {"start": v(15.95, -370) * mm, "end": v(15.95, -470) * mm});
            skLineSegment(sketch, "E74.6.6.6", {"start": v(-4.05, -370) * mm, "end": v(-4.05, -470) * mm});
            skLineSegment(sketch, "E74.9.6.6", {"start": v(15.95, -370) * mm, "end": v(-4.05, -370) * mm});
            skLineSegment(sketch, "E74.0.7.0", {"start": v(-34.05, 370) * mm, "end": v(-54.05, 370) * mm});
            skLineSegment(sketch, "E74.3.7.0", {"start": v(-34.05, 470) * mm, "end": v(-34.05, 370) * mm});
            skLineSegment(sketch, "E74.6.7.0", {"start": v(-54.05, 470) * mm, "end": v(-54.05, 370) * mm});
            skLineSegment(sketch, "E74.9.7.0", {"start": v(-34.05, 470) * mm, "end": v(-54.05, 470) * mm});
            skLineSegment(sketch, "E74.0.7.1", {"start": v(-34.05, 230) * mm, "end": v(-54.05, 230) * mm});
            skLineSegment(sketch, "E74.3.7.1", {"start": v(-34.05, 330) * mm, "end": v(-34.05, 230) * mm});
            skLineSegment(sketch, "E74.6.7.1", {"start": v(-54.05, 330) * mm, "end": v(-54.05, 230) * mm});
            skLineSegment(sketch, "E74.9.7.1", {"start": v(-34.05, 330) * mm, "end": v(-54.05, 330) * mm});
            skLineSegment(sketch, "E74.0.7.2", {"start": v(-34.05, 90) * mm, "end": v(-54.05, 90) * mm});
            skLineSegment(sketch, "E74.3.7.2", {"start": v(-34.05, 190) * mm, "end": v(-34.05, 90) * mm});
            skLineSegment(sketch, "E74.6.7.2", {"start": v(-54.05, 190) * mm, "end": v(-54.05, 90) * mm});
            skLineSegment(sketch, "E74.9.7.2", {"start": v(-34.05, 190) * mm, "end": v(-54.05, 190) * mm});
            skLineSegment(sketch, "E74.0.7.3", {"start": v(-34.05, -50) * mm, "end": v(-54.05, -50) * mm});
            skLineSegment(sketch, "E74.3.7.3", {"start": v(-34.05, 50) * mm, "end": v(-34.05, -50) * mm});
            skLineSegment(sketch, "E74.6.7.3", {"start": v(-54.05, 50) * mm, "end": v(-54.05, -50) * mm});
            skLineSegment(sketch, "E74.9.7.3", {"start": v(-34.05, 50) * mm, "end": v(-54.05, 50) * mm});
            skLineSegment(sketch, "E74.0.7.4", {"start": v(-34.05, -190) * mm, "end": v(-54.05, -190) * mm});
            skLineSegment(sketch, "E74.3.7.4", {"start": v(-34.05, -90) * mm, "end": v(-34.05, -190) * mm});
            skLineSegment(sketch, "E74.6.7.4", {"start": v(-54.05, -90) * mm, "end": v(-54.05, -190) * mm});
            skLineSegment(sketch, "E74.9.7.4", {"start": v(-34.05, -90) * mm, "end": v(-54.05, -90) * mm});
            skLineSegment(sketch, "E74.0.7.5", {"start": v(-34.05, -330) * mm, "end": v(-54.05, -330) * mm});
            skLineSegment(sketch, "E74.3.7.5", {"start": v(-34.05, -230) * mm, "end": v(-34.05, -330) * mm});
            skLineSegment(sketch, "E74.6.7.5", {"start": v(-54.05, -230) * mm, "end": v(-54.05, -330) * mm});
            skLineSegment(sketch, "E74.9.7.5", {"start": v(-34.05, -230) * mm, "end": v(-54.05, -230) * mm});
            skLineSegment(sketch, "E74.0.7.6", {"start": v(-34.05, -470) * mm, "end": v(-54.05, -470) * mm});
            skLineSegment(sketch, "E74.3.7.6", {"start": v(-34.05, -370) * mm, "end": v(-34.05, -470) * mm});
            skLineSegment(sketch, "E74.6.7.6", {"start": v(-54.05, -370) * mm, "end": v(-54.05, -470) * mm});
            skLineSegment(sketch, "E74.9.7.6", {"start": v(-34.05, -370) * mm, "end": v(-54.05, -370) * mm});
            skLineSegment(sketch, "E74.0.8.0", {"start": v(-84.05, 370) * mm, "end": v(-104.05, 370) * mm});
            skLineSegment(sketch, "E74.3.8.0", {"start": v(-84.05, 470) * mm, "end": v(-84.05, 370) * mm});
            skLineSegment(sketch, "E74.6.8.0", {"start": v(-104.05, 470) * mm, "end": v(-104.05, 370) * mm});
            skLineSegment(sketch, "E74.9.8.0", {"start": v(-84.05, 470) * mm, "end": v(-104.05, 470) * mm});
            skLineSegment(sketch, "E74.0.8.1", {"start": v(-84.05, 230) * mm, "end": v(-104.05, 230) * mm});
            skLineSegment(sketch, "E74.3.8.1", {"start": v(-84.05, 330) * mm, "end": v(-84.05, 230) * mm});
            skLineSegment(sketch, "E74.6.8.1", {"start": v(-104.05, 330) * mm, "end": v(-104.05, 230) * mm});
            skLineSegment(sketch, "E74.9.8.1", {"start": v(-84.05, 330) * mm, "end": v(-104.05, 330) * mm});
            skLineSegment(sketch, "E74.0.8.2", {"start": v(-84.05, 90) * mm, "end": v(-104.05, 90) * mm});
            skLineSegment(sketch, "E74.3.8.2", {"start": v(-84.05, 190) * mm, "end": v(-84.05, 90) * mm});
            skLineSegment(sketch, "E74.6.8.2", {"start": v(-104.05, 190) * mm, "end": v(-104.05, 90) * mm});
            skLineSegment(sketch, "E74.9.8.2", {"start": v(-84.05, 190) * mm, "end": v(-104.05, 190) * mm});
            skLineSegment(sketch, "E74.0.8.3", {"start": v(-84.05, -50) * mm, "end": v(-104.05, -50) * mm});
            skLineSegment(sketch, "E74.3.8.3", {"start": v(-84.05, 50) * mm, "end": v(-84.05, -50) * mm});
            skLineSegment(sketch, "E74.6.8.3", {"start": v(-104.05, 50) * mm, "end": v(-104.05, -50) * mm});
            skLineSegment(sketch, "E74.9.8.3", {"start": v(-84.05, 50) * mm, "end": v(-104.05, 50) * mm});
            skLineSegment(sketch, "E74.0.8.4", {"start": v(-84.05, -190) * mm, "end": v(-104.05, -190) * mm});
            skLineSegment(sketch, "E74.3.8.4", {"start": v(-84.05, -90) * mm, "end": v(-84.05, -190) * mm});
            skLineSegment(sketch, "E74.6.8.4", {"start": v(-104.05, -90) * mm, "end": v(-104.05, -190) * mm});
            skLineSegment(sketch, "E74.9.8.4", {"start": v(-84.05, -90) * mm, "end": v(-104.05, -90) * mm});
            skLineSegment(sketch, "E74.0.8.5", {"start": v(-84.05, -330) * mm, "end": v(-104.05, -330) * mm});
            skLineSegment(sketch, "E74.3.8.5", {"start": v(-84.05, -230) * mm, "end": v(-84.05, -330) * mm});
            skLineSegment(sketch, "E74.6.8.5", {"start": v(-104.05, -230) * mm, "end": v(-104.05, -330) * mm});
            skLineSegment(sketch, "E74.9.8.5", {"start": v(-84.05, -230) * mm, "end": v(-104.05, -230) * mm});
            skLineSegment(sketch, "E74.0.8.6", {"start": v(-84.05, -470) * mm, "end": v(-104.05, -470) * mm});
            skLineSegment(sketch, "E74.3.8.6", {"start": v(-84.05, -370) * mm, "end": v(-84.05, -470) * mm});
            skLineSegment(sketch, "E74.6.8.6", {"start": v(-104.05, -370) * mm, "end": v(-104.05, -470) * mm});
            skLineSegment(sketch, "E74.9.8.6", {"start": v(-84.05, -370) * mm, "end": v(-104.05, -370) * mm});
            skLineSegment(sketch, "E74.0.9.0", {"start": v(-134.05, 370) * mm, "end": v(-154.05, 370) * mm});
            skLineSegment(sketch, "E74.3.9.0", {"start": v(-134.05, 470) * mm, "end": v(-134.05, 370) * mm});
            skLineSegment(sketch, "E74.6.9.0", {"start": v(-154.05, 470) * mm, "end": v(-154.05, 370) * mm});
            skLineSegment(sketch, "E74.9.9.0", {"start": v(-134.05, 470) * mm, "end": v(-154.05, 470) * mm});
            skLineSegment(sketch, "E74.0.9.1", {"start": v(-134.05, 230) * mm, "end": v(-154.05, 230) * mm});
            skLineSegment(sketch, "E74.3.9.1", {"start": v(-134.05, 330) * mm, "end": v(-134.05, 230) * mm});
            skLineSegment(sketch, "E74.6.9.1", {"start": v(-154.05, 330) * mm, "end": v(-154.05, 230) * mm});
            skLineSegment(sketch, "E74.9.9.1", {"start": v(-134.05, 330) * mm, "end": v(-154.05, 330) * mm});
            skLineSegment(sketch, "E74.0.9.2", {"start": v(-134.05, 90) * mm, "end": v(-154.05, 90) * mm});
            skLineSegment(sketch, "E74.3.9.2", {"start": v(-134.05, 190) * mm, "end": v(-134.05, 90) * mm});
            skLineSegment(sketch, "E74.6.9.2", {"start": v(-154.05, 190) * mm, "end": v(-154.05, 90) * mm});
            skLineSegment(sketch, "E74.9.9.2", {"start": v(-134.05, 190) * mm, "end": v(-154.05, 190) * mm});
            skLineSegment(sketch, "E74.0.9.3", {"start": v(-134.05, -50) * mm, "end": v(-154.05, -50) * mm});
            skLineSegment(sketch, "E74.3.9.3", {"start": v(-134.05, 50) * mm, "end": v(-134.05, -50) * mm});
            skLineSegment(sketch, "E74.6.9.3", {"start": v(-154.05, 50) * mm, "end": v(-154.05, -50) * mm});
            skLineSegment(sketch, "E74.9.9.3", {"start": v(-134.05, 50) * mm, "end": v(-154.05, 50) * mm});
            skLineSegment(sketch, "E74.0.9.4", {"start": v(-134.05, -190) * mm, "end": v(-154.05, -190) * mm});
            skLineSegment(sketch, "E74.3.9.4", {"start": v(-134.05, -90) * mm, "end": v(-134.05, -190) * mm});
            skLineSegment(sketch, "E74.6.9.4", {"start": v(-154.05, -90) * mm, "end": v(-154.05, -190) * mm});
            skLineSegment(sketch, "E74.9.9.4", {"start": v(-134.05, -90) * mm, "end": v(-154.05, -90) * mm});
            skLineSegment(sketch, "E74.0.9.5", {"start": v(-134.05, -330) * mm, "end": v(-154.05, -330) * mm});
            skLineSegment(sketch, "E74.3.9.5", {"start": v(-134.05, -230) * mm, "end": v(-134.05, -330) * mm});
            skLineSegment(sketch, "E74.6.9.5", {"start": v(-154.05, -230) * mm, "end": v(-154.05, -330) * mm});
            skLineSegment(sketch, "E74.9.9.5", {"start": v(-134.05, -230) * mm, "end": v(-154.05, -230) * mm});
            skLineSegment(sketch, "E74.0.9.6", {"start": v(-134.05, -470) * mm, "end": v(-154.05, -470) * mm});
            skLineSegment(sketch, "E74.3.9.6", {"start": v(-134.05, -370) * mm, "end": v(-134.05, -470) * mm});
            skLineSegment(sketch, "E74.6.9.6", {"start": v(-154.05, -370) * mm, "end": v(-154.05, -470) * mm});
            skLineSegment(sketch, "E74.9.9.6", {"start": v(-134.05, -370) * mm, "end": v(-154.05, -370) * mm});
            skLineSegment(sketch, "E74.0.10.0", {"start": v(-184.05, 370) * mm, "end": v(-204.05, 370) * mm});
            skLineSegment(sketch, "E74.3.10.0", {"start": v(-184.05, 470) * mm, "end": v(-184.05, 370) * mm});
            skLineSegment(sketch, "E74.6.10.0", {"start": v(-204.05, 470) * mm, "end": v(-204.05, 370) * mm});
            skLineSegment(sketch, "E74.9.10.0", {"start": v(-184.05, 470) * mm, "end": v(-204.05, 470) * mm});
            skLineSegment(sketch, "E74.0.10.1", {"start": v(-184.05, 230) * mm, "end": v(-204.05, 230) * mm});
            skLineSegment(sketch, "E74.3.10.1", {"start": v(-184.05, 330) * mm, "end": v(-184.05, 230) * mm});
            skLineSegment(sketch, "E74.6.10.1", {"start": v(-204.05, 330) * mm, "end": v(-204.05, 230) * mm});
            skLineSegment(sketch, "E74.9.10.1", {"start": v(-184.05, 330) * mm, "end": v(-204.05, 330) * mm});
            skLineSegment(sketch, "E74.0.10.2", {"start": v(-184.05, 90) * mm, "end": v(-204.05, 90) * mm});
            skLineSegment(sketch, "E74.3.10.2", {"start": v(-184.05, 190) * mm, "end": v(-184.05, 90) * mm});
            skLineSegment(sketch, "E74.6.10.2", {"start": v(-204.05, 190) * mm, "end": v(-204.05, 90) * mm});
            skLineSegment(sketch, "E74.9.10.2", {"start": v(-184.05, 190) * mm, "end": v(-204.05, 190) * mm});
            skLineSegment(sketch, "E74.0.10.3", {"start": v(-184.05, -50) * mm, "end": v(-204.05, -50) * mm});
            skLineSegment(sketch, "E74.3.10.3", {"start": v(-184.05, 50) * mm, "end": v(-184.05, -50) * mm});
            skLineSegment(sketch, "E74.6.10.3", {"start": v(-204.05, 50) * mm, "end": v(-204.05, -50) * mm});
            skLineSegment(sketch, "E74.9.10.3", {"start": v(-184.05, 50) * mm, "end": v(-204.05, 50) * mm});
            skLineSegment(sketch, "E74.0.10.4", {"start": v(-184.05, -190) * mm, "end": v(-204.05, -190) * mm});
            skLineSegment(sketch, "E74.3.10.4", {"start": v(-184.05, -90) * mm, "end": v(-184.05, -190) * mm});
            skLineSegment(sketch, "E74.6.10.4", {"start": v(-204.05, -90) * mm, "end": v(-204.05, -190) * mm});
            skLineSegment(sketch, "E74.9.10.4", {"start": v(-184.05, -90) * mm, "end": v(-204.05, -90) * mm});
            skLineSegment(sketch, "E74.0.10.5", {"start": v(-184.05, -330) * mm, "end": v(-204.05, -330) * mm});
            skLineSegment(sketch, "E74.3.10.5", {"start": v(-184.05, -230) * mm, "end": v(-184.05, -330) * mm});
            skLineSegment(sketch, "E74.6.10.5", {"start": v(-204.05, -230) * mm, "end": v(-204.05, -330) * mm});
            skLineSegment(sketch, "E74.9.10.5", {"start": v(-184.05, -230) * mm, "end": v(-204.05, -230) * mm});
            skLineSegment(sketch, "E74.0.10.6", {"start": v(-184.05, -470) * mm, "end": v(-204.05, -470) * mm});
            skLineSegment(sketch, "E74.3.10.6", {"start": v(-184.05, -370) * mm, "end": v(-184.05, -470) * mm});
            skLineSegment(sketch, "E74.6.10.6", {"start": v(-204.05, -370) * mm, "end": v(-204.05, -470) * mm});
            skLineSegment(sketch, "E74.9.10.6", {"start": v(-184.05, -370) * mm, "end": v(-204.05, -370) * mm});
            skLineSegment(sketch, "E74.0.11.0", {"start": v(-234.05, 370) * mm, "end": v(-254.05, 370) * mm});
            skLineSegment(sketch, "E74.3.11.0", {"start": v(-234.05, 470) * mm, "end": v(-234.05, 370) * mm});
            skLineSegment(sketch, "E74.6.11.0", {"start": v(-254.05, 470) * mm, "end": v(-254.05, 370) * mm});
            skLineSegment(sketch, "E74.9.11.0", {"start": v(-234.05, 470) * mm, "end": v(-254.05, 470) * mm});
            skLineSegment(sketch, "E74.0.11.1", {"start": v(-234.05, 230) * mm, "end": v(-254.05, 230) * mm});
            skLineSegment(sketch, "E74.3.11.1", {"start": v(-234.05, 330) * mm, "end": v(-234.05, 230) * mm});
            skLineSegment(sketch, "E74.6.11.1", {"start": v(-254.05, 330) * mm, "end": v(-254.05, 230) * mm});
            skLineSegment(sketch, "E74.9.11.1", {"start": v(-234.05, 330) * mm, "end": v(-254.05, 330) * mm});
            skLineSegment(sketch, "E74.0.11.2", {"start": v(-234.05, 90) * mm, "end": v(-254.05, 90) * mm});
            skLineSegment(sketch, "E74.3.11.2", {"start": v(-234.05, 190) * mm, "end": v(-234.05, 90) * mm});
            skLineSegment(sketch, "E74.6.11.2", {"start": v(-254.05, 190) * mm, "end": v(-254.05, 90) * mm});
            skLineSegment(sketch, "E74.9.11.2", {"start": v(-234.05, 190) * mm, "end": v(-254.05, 190) * mm});
            skLineSegment(sketch, "E74.0.11.3", {"start": v(-234.05, -50) * mm, "end": v(-254.05, -50) * mm});
            skLineSegment(sketch, "E74.3.11.3", {"start": v(-234.05, 50) * mm, "end": v(-234.05, -50) * mm});
            skLineSegment(sketch, "E74.6.11.3", {"start": v(-254.05, 50) * mm, "end": v(-254.05, -50) * mm});
            skLineSegment(sketch, "E74.9.11.3", {"start": v(-234.05, 50) * mm, "end": v(-254.05, 50) * mm});
            skLineSegment(sketch, "E74.0.11.4", {"start": v(-234.05, -190) * mm, "end": v(-254.05, -190) * mm});
            skLineSegment(sketch, "E74.3.11.4", {"start": v(-234.05, -90) * mm, "end": v(-234.05, -190) * mm});
            skLineSegment(sketch, "E74.6.11.4", {"start": v(-254.05, -90) * mm, "end": v(-254.05, -190) * mm});
            skLineSegment(sketch, "E74.9.11.4", {"start": v(-234.05, -90) * mm, "end": v(-254.05, -90) * mm});
            skLineSegment(sketch, "E74.0.11.5", {"start": v(-234.05, -330) * mm, "end": v(-254.05, -330) * mm});
            skLineSegment(sketch, "E74.3.11.5", {"start": v(-234.05, -230) * mm, "end": v(-234.05, -330) * mm});
            skLineSegment(sketch, "E74.6.11.5", {"start": v(-254.05, -230) * mm, "end": v(-254.05, -330) * mm});
            skLineSegment(sketch, "E74.9.11.5", {"start": v(-234.05, -230) * mm, "end": v(-254.05, -230) * mm});
            skLineSegment(sketch, "E74.0.11.6", {"start": v(-234.05, -470) * mm, "end": v(-254.05, -470) * mm});
            skLineSegment(sketch, "E74.3.11.6", {"start": v(-234.05, -370) * mm, "end": v(-234.05, -470) * mm});
            skLineSegment(sketch, "E74.6.11.6", {"start": v(-254.05, -370) * mm, "end": v(-254.05, -470) * mm});
            skLineSegment(sketch, "E74.9.11.6", {"start": v(-234.05, -370) * mm, "end": v(-254.05, -370) * mm});
            skLineSegment(sketch, "E74.0.12.0", {"start": v(-284.05, 370) * mm, "end": v(-304.05, 370) * mm});
            skLineSegment(sketch, "E74.3.12.0", {"start": v(-284.05, 470) * mm, "end": v(-284.05, 370) * mm});
            skLineSegment(sketch, "E74.6.12.0", {"start": v(-304.05, 470) * mm, "end": v(-304.05, 370) * mm});
            skLineSegment(sketch, "E74.9.12.0", {"start": v(-284.05, 470) * mm, "end": v(-304.05, 470) * mm});
            skLineSegment(sketch, "E74.0.12.1", {"start": v(-284.05, 230) * mm, "end": v(-304.05, 230) * mm});
            skLineSegment(sketch, "E74.3.12.1", {"start": v(-284.05, 330) * mm, "end": v(-284.05, 230) * mm});
            skLineSegment(sketch, "E74.6.12.1", {"start": v(-304.05, 330) * mm, "end": v(-304.05, 230) * mm});
            skLineSegment(sketch, "E74.9.12.1", {"start": v(-284.05, 330) * mm, "end": v(-304.05, 330) * mm});
            skLineSegment(sketch, "E74.0.12.2", {"start": v(-284.05, 90) * mm, "end": v(-304.05, 90) * mm});
            skLineSegment(sketch, "E74.3.12.2", {"start": v(-284.05, 190) * mm, "end": v(-284.05, 90) * mm});
            skLineSegment(sketch, "E74.6.12.2", {"start": v(-304.05, 190) * mm, "end": v(-304.05, 90) * mm});
            skLineSegment(sketch, "E74.9.12.2", {"start": v(-284.05, 190) * mm, "end": v(-304.05, 190) * mm});
            skLineSegment(sketch, "E74.0.12.3", {"start": v(-284.05, -50) * mm, "end": v(-304.05, -50) * mm});
            skLineSegment(sketch, "E74.3.12.3", {"start": v(-284.05, 50) * mm, "end": v(-284.05, -50) * mm});
            skLineSegment(sketch, "E74.6.12.3", {"start": v(-304.05, 50) * mm, "end": v(-304.05, -50) * mm});
            skLineSegment(sketch, "E74.9.12.3", {"start": v(-284.05, 50) * mm, "end": v(-304.05, 50) * mm});
            skLineSegment(sketch, "E74.0.12.4", {"start": v(-284.05, -190) * mm, "end": v(-304.05, -190) * mm});
            skLineSegment(sketch, "E74.3.12.4", {"start": v(-284.05, -90) * mm, "end": v(-284.05, -190) * mm});
            skLineSegment(sketch, "E74.6.12.4", {"start": v(-304.05, -90) * mm, "end": v(-304.05, -190) * mm});
            skLineSegment(sketch, "E74.9.12.4", {"start": v(-284.05, -90) * mm, "end": v(-304.05, -90) * mm});
            skLineSegment(sketch, "E74.0.12.5", {"start": v(-284.05, -330) * mm, "end": v(-304.05, -330) * mm});
            skLineSegment(sketch, "E74.3.12.5", {"start": v(-284.05, -230) * mm, "end": v(-284.05, -330) * mm});
            skLineSegment(sketch, "E74.6.12.5", {"start": v(-304.05, -230) * mm, "end": v(-304.05, -330) * mm});
            skLineSegment(sketch, "E74.9.12.5", {"start": v(-284.05, -230) * mm, "end": v(-304.05, -230) * mm});
            skLineSegment(sketch, "E74.0.12.6", {"start": v(-284.05, -470) * mm, "end": v(-304.05, -470) * mm});
            skLineSegment(sketch, "E74.3.12.6", {"start": v(-284.05, -370) * mm, "end": v(-284.05, -470) * mm});
            skLineSegment(sketch, "E74.6.12.6", {"start": v(-304.05, -370) * mm, "end": v(-304.05, -470) * mm});
            skLineSegment(sketch, "E74.9.12.6", {"start": v(-284.05, -370) * mm, "end": v(-304.05, -370) * mm});
            skLineSegment(sketch, "E74.0.13.0", {"start": v(-334.05, 370) * mm, "end": v(-354.05, 370) * mm});
            skLineSegment(sketch, "E74.3.13.0", {"start": v(-334.05, 470) * mm, "end": v(-334.05, 370) * mm});
            skLineSegment(sketch, "E74.6.13.0", {"start": v(-354.05, 470) * mm, "end": v(-354.05, 370) * mm});
            skLineSegment(sketch, "E74.9.13.0", {"start": v(-334.05, 470) * mm, "end": v(-354.05, 470) * mm});
            skLineSegment(sketch, "E74.0.13.1", {"start": v(-334.05, 230) * mm, "end": v(-354.05, 230) * mm});
            skLineSegment(sketch, "E74.3.13.1", {"start": v(-334.05, 330) * mm, "end": v(-334.05, 230) * mm});
            skLineSegment(sketch, "E74.6.13.1", {"start": v(-354.05, 330) * mm, "end": v(-354.05, 230) * mm});
            skLineSegment(sketch, "E74.9.13.1", {"start": v(-334.05, 330) * mm, "end": v(-354.05, 330) * mm});
            skLineSegment(sketch, "E74.0.13.2", {"start": v(-334.05, 90) * mm, "end": v(-354.05, 90) * mm});
            skLineSegment(sketch, "E74.3.13.2", {"start": v(-334.05, 190) * mm, "end": v(-334.05, 90) * mm});
            skLineSegment(sketch, "E74.6.13.2", {"start": v(-354.05, 190) * mm, "end": v(-354.05, 90) * mm});
            skLineSegment(sketch, "E74.9.13.2", {"start": v(-334.05, 190) * mm, "end": v(-354.05, 190) * mm});
            skLineSegment(sketch, "E74.0.13.3", {"start": v(-334.05, -50) * mm, "end": v(-354.05, -50) * mm});
            skLineSegment(sketch, "E74.3.13.3", {"start": v(-334.05, 50) * mm, "end": v(-334.05, -50) * mm});
            skLineSegment(sketch, "E74.6.13.3", {"start": v(-354.05, 50) * mm, "end": v(-354.05, -50) * mm});
            skLineSegment(sketch, "E74.9.13.3", {"start": v(-334.05, 50) * mm, "end": v(-354.05, 50) * mm});
            skLineSegment(sketch, "E74.0.13.4", {"start": v(-334.05, -190) * mm, "end": v(-354.05, -190) * mm});
            skLineSegment(sketch, "E74.3.13.4", {"start": v(-334.05, -90) * mm, "end": v(-334.05, -190) * mm});
            skLineSegment(sketch, "E74.6.13.4", {"start": v(-354.05, -90) * mm, "end": v(-354.05, -190) * mm});
            skLineSegment(sketch, "E74.9.13.4", {"start": v(-334.05, -90) * mm, "end": v(-354.05, -90) * mm});
            skLineSegment(sketch, "E74.0.13.5", {"start": v(-334.05, -330) * mm, "end": v(-354.05, -330) * mm});
            skLineSegment(sketch, "E74.3.13.5", {"start": v(-334.05, -230) * mm, "end": v(-334.05, -330) * mm});
            skLineSegment(sketch, "E74.6.13.5", {"start": v(-354.05, -230) * mm, "end": v(-354.05, -330) * mm});
            skLineSegment(sketch, "E74.9.13.5", {"start": v(-334.05, -230) * mm, "end": v(-354.05, -230) * mm});
            skLineSegment(sketch, "E74.0.13.6", {"start": v(-334.05, -470) * mm, "end": v(-354.05, -470) * mm});
            skLineSegment(sketch, "E74.3.13.6", {"start": v(-334.05, -370) * mm, "end": v(-334.05, -470) * mm});
            skLineSegment(sketch, "E74.6.13.6", {"start": v(-354.05, -370) * mm, "end": v(-354.05, -470) * mm});
            skLineSegment(sketch, "E74.9.13.6", {"start": v(-334.05, -370) * mm, "end": v(-354.05, -370) * mm});
            skLineSegment(sketch, "E74.0.14.0", {"start": v(-384.05, 370) * mm, "end": v(-404.05, 370) * mm});
            skLineSegment(sketch, "E74.3.14.0", {"start": v(-384.05, 470) * mm, "end": v(-384.05, 370) * mm});
            skLineSegment(sketch, "E74.6.14.0", {"start": v(-404.05, 470) * mm, "end": v(-404.05, 370) * mm});
            skLineSegment(sketch, "E74.9.14.0", {"start": v(-384.05, 470) * mm, "end": v(-404.05, 470) * mm});
            skLineSegment(sketch, "E74.0.14.1", {"start": v(-384.05, 230) * mm, "end": v(-404.05, 230) * mm});
            skLineSegment(sketch, "E74.3.14.1", {"start": v(-384.05, 330) * mm, "end": v(-384.05, 230) * mm});
            skLineSegment(sketch, "E74.6.14.1", {"start": v(-404.05, 330) * mm, "end": v(-404.05, 230) * mm});
            skLineSegment(sketch, "E74.9.14.1", {"start": v(-384.05, 330) * mm, "end": v(-404.05, 330) * mm});
            skLineSegment(sketch, "E74.0.14.2", {"start": v(-384.05, 90) * mm, "end": v(-404.05, 90) * mm});
            skLineSegment(sketch, "E74.3.14.2", {"start": v(-384.05, 190) * mm, "end": v(-384.05, 90) * mm});
            skLineSegment(sketch, "E74.6.14.2", {"start": v(-404.05, 190) * mm, "end": v(-404.05, 90) * mm});
            skLineSegment(sketch, "E74.9.14.2", {"start": v(-384.05, 190) * mm, "end": v(-404.05, 190) * mm});
            skLineSegment(sketch, "E74.0.14.3", {"start": v(-384.05, -50) * mm, "end": v(-404.05, -50) * mm});
            skLineSegment(sketch, "E74.3.14.3", {"start": v(-384.05, 50) * mm, "end": v(-384.05, -50) * mm});
            skLineSegment(sketch, "E74.6.14.3", {"start": v(-404.05, 50) * mm, "end": v(-404.05, -50) * mm});
            skLineSegment(sketch, "E74.9.14.3", {"start": v(-384.05, 50) * mm, "end": v(-404.05, 50) * mm});
            skLineSegment(sketch, "E74.0.14.4", {"start": v(-384.05, -190) * mm, "end": v(-404.05, -190) * mm});
            skLineSegment(sketch, "E74.3.14.4", {"start": v(-384.05, -90) * mm, "end": v(-384.05, -190) * mm});
            skLineSegment(sketch, "E74.6.14.4", {"start": v(-404.05, -90) * mm, "end": v(-404.05, -190) * mm});
            skLineSegment(sketch, "E74.9.14.4", {"start": v(-384.05, -90) * mm, "end": v(-404.05, -90) * mm});
            skLineSegment(sketch, "E74.0.14.5", {"start": v(-384.05, -330) * mm, "end": v(-404.05, -330) * mm});
            skLineSegment(sketch, "E74.3.14.5", {"start": v(-384.05, -230) * mm, "end": v(-384.05, -330) * mm});
            skLineSegment(sketch, "E74.6.14.5", {"start": v(-404.05, -230) * mm, "end": v(-404.05, -330) * mm});
            skLineSegment(sketch, "E74.9.14.5", {"start": v(-384.05, -230) * mm, "end": v(-404.05, -230) * mm});
            skLineSegment(sketch, "E74.0.14.6", {"start": v(-384.05, -470) * mm, "end": v(-404.05, -470) * mm});
            skLineSegment(sketch, "E74.3.14.6", {"start": v(-384.05, -370) * mm, "end": v(-384.05, -470) * mm});
            skLineSegment(sketch, "E74.6.14.6", {"start": v(-404.05, -370) * mm, "end": v(-404.05, -470) * mm});
            skLineSegment(sketch, "E74.9.14.6", {"start": v(-384.05, -370) * mm, "end": v(-404.05, -370) * mm});
            skLineSegment(sketch, "E75.0.15.0", {"start": v(-434.05, 370) * mm, "end": v(-454.05, 370) * mm});
            skLineSegment(sketch, "E75.3.15.0", {"start": v(-434.05, 470) * mm, "end": v(-434.05, 370) * mm});
            skLineSegment(sketch, "E75.6.15.0", {"start": v(-454.05, 470) * mm, "end": v(-454.05, 370) * mm});
            skLineSegment(sketch, "E75.9.15.0", {"start": v(-434.05, 470) * mm, "end": v(-454.05, 470) * mm});
            skLineSegment(sketch, "E75.0.15.1", {"start": v(-434.05, 230) * mm, "end": v(-454.05, 230) * mm});
            skLineSegment(sketch, "E75.3.15.1", {"start": v(-434.05, 330) * mm, "end": v(-434.05, 230) * mm});
            skLineSegment(sketch, "E75.6.15.1", {"start": v(-454.05, 330) * mm, "end": v(-454.05, 230) * mm});
            skLineSegment(sketch, "E75.9.15.1", {"start": v(-434.05, 330) * mm, "end": v(-454.05, 330) * mm});
            skLineSegment(sketch, "E75.0.15.2", {"start": v(-434.05, 90) * mm, "end": v(-454.05, 90) * mm});
            skLineSegment(sketch, "E75.3.15.2", {"start": v(-434.05, 190) * mm, "end": v(-434.05, 90) * mm});
            skLineSegment(sketch, "E75.6.15.2", {"start": v(-454.05, 190) * mm, "end": v(-454.05, 90) * mm});
            skLineSegment(sketch, "E75.9.15.2", {"start": v(-434.05, 190) * mm, "end": v(-454.05, 190) * mm});
            skLineSegment(sketch, "E75.0.15.3", {"start": v(-434.05, -50) * mm, "end": v(-454.05, -50) * mm});
            skLineSegment(sketch, "E75.3.15.3", {"start": v(-434.05, 50) * mm, "end": v(-434.05, -50) * mm});
            skLineSegment(sketch, "E75.6.15.3", {"start": v(-454.05, 50) * mm, "end": v(-454.05, -50) * mm});
            skLineSegment(sketch, "E75.9.15.3", {"start": v(-434.05, 50) * mm, "end": v(-454.05, 50) * mm});
            skLineSegment(sketch, "E75.0.15.4", {"start": v(-434.05, -190) * mm, "end": v(-454.05, -190) * mm});
            skLineSegment(sketch, "E75.3.15.4", {"start": v(-434.05, -90) * mm, "end": v(-434.05, -190) * mm});
            skLineSegment(sketch, "E75.6.15.4", {"start": v(-454.05, -90) * mm, "end": v(-454.05, -190) * mm});
            skLineSegment(sketch, "E75.9.15.4", {"start": v(-434.05, -90) * mm, "end": v(-454.05, -90) * mm});
            skLineSegment(sketch, "E75.0.15.5", {"start": v(-434.05, -330) * mm, "end": v(-454.05, -330) * mm});
            skLineSegment(sketch, "E75.3.15.5", {"start": v(-434.05, -230) * mm, "end": v(-434.05, -330) * mm});
            skLineSegment(sketch, "E75.6.15.5", {"start": v(-454.05, -230) * mm, "end": v(-454.05, -330) * mm});
            skLineSegment(sketch, "E75.9.15.5", {"start": v(-434.05, -230) * mm, "end": v(-454.05, -230) * mm});
            skLineSegment(sketch, "E75.0.15.6", {"start": v(-434.05, -470) * mm, "end": v(-454.05, -470) * mm});
            skLineSegment(sketch, "E75.3.15.6", {"start": v(-434.05, -370) * mm, "end": v(-434.05, -470) * mm});
            skLineSegment(sketch, "E75.6.15.6", {"start": v(-454.05, -370) * mm, "end": v(-454.05, -470) * mm});
            skLineSegment(sketch, "E75.9.15.6", {"start": v(-434.05, -370) * mm, "end": v(-454.05, -370) * mm});
            skSolve(sketch);
        }
        {
            var Q0;
            Q0 = qSketchRegion(id + "F17", true);
            var Q1;
            Q1=makeQuery(id+"F16.opExtrude","SWEPT_FACE",FACE,{"disambiguationData":[OSD([sQuery(id+"F15.wireOp",EDGE,"E61")])]});
            extrude(context, id + "F18", {"entities" : qUnion([Q0]), "operationType" : NewBodyOperationType.REMOVE, "endBound" : BoundingType.UP_TO_SURFACE, "oppositeDirection" : true, "depth" : 25 * mm, "endBoundEntityFace" : qUnion([Q1]), "offsetDistance" : 25 * mm});
        }
        {
            var Q0;
            Q0=qCreatedBy(makeId("Front.planeOp"),FACE);
            var sketch = newSketch(context, id + "F19", { "sketchPlane" : qUnion([Q0])});
            skLineSegment(sketch, "E76.0", {"start": v(250, -500) * mm, "end": v(207.26, -195.89) * mm});
            skLineSegment(sketch, "E76.5", {"start": v(207.26, -195.89) * mm, "end": v(-573.67, -100) * mm});
            skLineSegment(sketch, "E77", {"start": v(-432.74, -89.1) * mm, "end": v(-421.77, 0.23) * mm});
            skLineSegment(sketch, "E78", {"start": v(-421.77, 0.23) * mm, "end": v(402.34, -100.95) * mm});
            skLineSegment(sketch, "E79.0", {"start": v(600, -500) * mm, "end": v(250, -500) * mm});
            skLineSegment(sketch, "E80.0", {"start": v(511.32, 131.02) * mm, "end": v(600, -500) * mm});
            skLineSegment(sketch, "E81", {"start": v(388.86, -169.82) * mm, "end": v(453.5, -228.66) * mm});
            skLineSegment(sketch, "E82", {"start": v(457.3, -255.72) * mm, "end": v(516.71, -247.37) * mm});
            skLineSegment(sketch, "E83", {"start": v(516.71, -247.37) * mm, "end": v(509.9, -198.87) * mm});
            skLineSegment(sketch, "E84.0", {"start": v(433.06, 147.65) * mm, "end": v(511.32, 131.02) * mm});
            skLineSegment(sketch, "E84.1", {"start": v(433.06, 247.65) * mm, "end": v(433.06, 147.65) * mm});
            skLineSegment(sketch, "E84.2", {"start": v(433.06, 247.65) * mm, "end": v(221.32, 500) * mm});
            skLineSegment(sketch, "E85.0", {"start": v(-500, 500) * mm, "end": v(-573.67, -100) * mm});
            skLineSegment(sketch, "E86", {"start": v(-503.23, 177.69) * mm, "end": v(-511.76, 108.2) * mm});
            skLineSegment(sketch, "E87", {"start": v(-511.76, 108.2) * mm, "end": v(366.17, 0.41) * mm});
            skLineSegment(sketch, "E88", {"start": v(366.17, 0.41) * mm, "end": v(458.25, -75.92) * mm});
            skLineSegment(sketch, "E89", {"start": v(458.25, -75.92) * mm, "end": v(496.54, -29.72) * mm});
            skLineSegment(sketch, "E90", {"start": v(496.54, -29.72) * mm, "end": v(376.66, 69.65) * mm});
            skLineSegment(sketch, "E91", {"start": v(376.66, 69.65) * mm, "end": v(-503.23, 177.69) * mm});
            skLineSegment(sketch, "E92", {"start": v(509.9, -198.87) * mm, "end": v(402.34, -100.95) * mm});
            skLineSegment(sketch, "E93", {"start": v(453.5, -228.66) * mm, "end": v(457.3, -255.72) * mm});
            skLineSegment(sketch, "E94", {"start": v(-363.26, -97.63) * mm, "end": v(-360.82, -77.77) * mm});
            skLineSegment(sketch, "E95", {"start": v(-360.82, -77.77) * mm, "end": v(388.86, -169.82) * mm});
            skLineSegment(sketch, "E96", {"start": v(-363.26, -97.63) * mm, "end": v(-432.74, -89.1) * mm});
            skLineSegment(sketch, "E97.1", {"start": v(526.97, -500) * mm, "end": v(491.95, -250.85) * mm});
            skLineSegment(sketch, "E98", {"start": v(458.25, -75.92) * mm, "end": v(470.5, -163) * mm});
            skLineSegment(sketch, "E99", {"start": v(-511.76, 108.2) * mm, "end": v(-547.57, 112.6) * mm});
            skLineSegment(sketch, "E100", {"start": v(496.54, -29.72) * mm, "end": v(533.18, -24.57) * mm});
            skLineSegment(sketch, "E101.0", {"start": v(221.32, 540) * mm, "end": v(221.32, 500) * mm});
            skLineSegment(sketch, "E101.1", {"start": v(221.32, 540) * mm, "end": v(-500, 540) * mm});
            skLineSegment(sketch, "E101.2", {"start": v(-500, 540) * mm, "end": v(-500, 500) * mm});
            skLineSegment(sketch, "E102", {"start": v(207.26, -195.89) * mm, "end": v(210.34, -196.26) * mm});
            skLineSegment(sketch, "E103", {"start": v(210.34, -196.26) * mm, "end": v(203.43, -147.06) * mm});
            skLineSegment(sketch, "E104.0", {"start": v(253.03, -500) * mm, "end": v(209.91, -193.19) * mm, "construction": true});
            skSolve(sketch);
        }
        {
            var Q0;
            Q0=qCreatedBy(makeId("Front.planeOp"),FACE);
            var sketch = newSketch(context, id + "F20", { "sketchPlane" : qUnion([Q0])});
            skLineSegment(sketch, "E105.0.8", {"start": v(207.26, -195.89) * mm, "end": v(250, -500) * mm});
            skLineSegment(sketch, "E106.1.2", {"start": v(-547.57, 112.6) * mm, "end": v(-573.67, -100) * mm});
            skLineSegment(sketch, "E106.1.3", {"start": v(-573.67, -100) * mm, "end": v(207.26, -195.89) * mm});
            skLineSegment(sketch, "E106.1.13", {"start": v(458.25, -75.92) * mm, "end": v(366.17, 0.41) * mm});
            skLineSegment(sketch, "E107.0.0", {"start": v(533.18, -24.57) * mm, "end": v(496.54, -29.72) * mm});
            skLineSegment(sketch, "E107.0.1", {"start": v(496.54, -29.72) * mm, "end": v(458.25, -75.92) * mm});
            skLineSegment(sketch, "E107.0.8", {"start": v(600, -500) * mm, "end": v(533.18, -24.57) * mm});
            skLineSegment(sketch, "E108", {"start": v(600, -500) * mm, "end": v(250, -500) * mm});
            skLineSegment(sketch, "E109", {"start": v(-547.57, 112.6) * mm, "end": v(366.17, 0.41) * mm});
            skSolve(sketch);
        }
        {
            var Q0;
            Q0 = qSketchRegion(id + "F20", true);
            var Q1;
            Q1=makeQuery(id+"F1.opExtrude","CAP_FACE",FACE,{"disambiguationData":[OSD([sQuery(id+"F0.wireOp",EDGE,"E1"),sQuery(id+"F0.wireOp",EDGE,"E2"),sQuery(id+"F0.wireOp",EDGE,"E3"),sQuery(id+"F0.wireOp",EDGE,"E4"),sQuery(id+"F0.wireOp",EDGE,"E5"),sQuery(id+"F0.wireOp",EDGE,"E6"),sQuery(id+"F0.wireOp",EDGE,"E7"),sQuery(id+"F0.wireOp",EDGE,"E8"),sQuery(id+"F0.wireOp",EDGE,"E9")])],"isStart":false});
            var Q2;
            Q2=makeQuery(id+"F1.opExtrude","CAP_FACE",FACE,{"disambiguationData":[OSD([sQuery(id+"F0.wireOp",EDGE,"E1"),sQuery(id+"F0.wireOp",EDGE,"E2"),sQuery(id+"F0.wireOp",EDGE,"E3"),sQuery(id+"F0.wireOp",EDGE,"E4"),sQuery(id+"F0.wireOp",EDGE,"E5"),sQuery(id+"F0.wireOp",EDGE,"E6"),sQuery(id+"F0.wireOp",EDGE,"E7"),sQuery(id+"F0.wireOp",EDGE,"E8"),sQuery(id+"F0.wireOp",EDGE,"E9")])],"isStart":true});
            extrude(context, id + "F21", {"entities" : qUnion([Q0]), "endBound" : BoundingType.UP_TO_SURFACE, "depth" : 25 * mm, "endBoundEntityFace" : qUnion([Q1]), "offsetDistance" : 25 * mm, "hasSecondDirection" : true, "secondDirectionBound" : SecondDirectionBoundingType.UP_TO_SURFACE, "secondDirectionOppositeDirection" : true, "secondDirectionDepth" : 25 * mm, "secondDirectionBoundEntityFace" : qUnion([Q2])});
        }
        {
            var Q0;
            Q0=qCreatedBy(makeId("Front.planeOp"),FACE);
            var sketch = newSketch(context, id + "F22", { "sketchPlane" : qUnion([Q0])});
            skLineSegment(sketch, "E110.0.0", {"start": v(376.66, 69.65) * mm, "end": v(496.54, -29.72) * mm});
            skLineSegment(sketch, "E110.0.1", {"start": v(496.54, -29.72) * mm, "end": v(533.18, -24.57) * mm});
            skLineSegment(sketch, "E110.0.2", {"start": v(533.18, -24.57) * mm, "end": v(511.32, 131.02) * mm});
            skLineSegment(sketch, "E110.0.3", {"start": v(511.32, 131.02) * mm, "end": v(433.06, 147.65) * mm});
            skLineSegment(sketch, "E110.0.4", {"start": v(433.06, 147.65) * mm, "end": v(433.06, 247.65) * mm});
            skLineSegment(sketch, "E110.0.5", {"start": v(433.06, 247.65) * mm, "end": v(221.32, 500) * mm});
            skLineSegment(sketch, "E110.0.6", {"start": v(221.32, 500) * mm, "end": v(221.32, 540) * mm});
            skLineSegment(sketch, "E110.0.7", {"start": v(221.32, 540) * mm, "end": v(-500, 540) * mm});
            skLineSegment(sketch, "E110.0.8", {"start": v(-500, 540) * mm, "end": v(-500, 500) * mm});
            skLineSegment(sketch, "E110.0.9", {"start": v(-500, 500) * mm, "end": v(-547.57, 112.6) * mm});
            skLineSegment(sketch, "E110.0.10", {"start": v(-547.57, 112.6) * mm, "end": v(-511.76, 108.2) * mm});
            skLineSegment(sketch, "E110.0.11", {"start": v(-511.76, 108.2) * mm, "end": v(-503.23, 177.69) * mm});
            skLineSegment(sketch, "E110.0.12", {"start": v(-503.23, 177.69) * mm, "end": v(376.66, 69.65) * mm});
            skSolve(sketch);
        }
        {
            var Q0;
            Q0 = qSketchRegion(id + "F22", true);
            var Q1;
            Q1=makeQuery(id+"F10.boolean.opBoolean","MERGE",FACE,{"derivedFrom":[makeQuery(id+"F1.opExtrude","CAP_FACE",FACE,{"disambiguationData":[OSD([sQuery(id+"F0.wireOp",EDGE,"E1"),sQuery(id+"F0.wireOp",EDGE,"E2"),sQuery(id+"F0.wireOp",EDGE,"E3"),sQuery(id+"F0.wireOp",EDGE,"E4"),sQuery(id+"F0.wireOp",EDGE,"E5"),sQuery(id+"F0.wireOp",EDGE,"E6"),sQuery(id+"F0.wireOp",EDGE,"E7"),sQuery(id+"F0.wireOp",EDGE,"E8"),sQuery(id+"F0.wireOp",EDGE,"E9")])],"isStart":false}),makeQuery(id+"F10.opExtrude","SWEPT_FACE",FACE,{"disambiguationData":[OSD([sQuery(id+"F9.wireOp",EDGE,"E39.0")])]})]});
            var Q2;
            Q2=makeQuery(id+"F10.boolean.opBoolean","MERGE",FACE,{"derivedFrom":[makeQuery(id+"F1.opExtrude","CAP_FACE",FACE,{"disambiguationData":[OSD([sQuery(id+"F0.wireOp",EDGE,"E1"),sQuery(id+"F0.wireOp",EDGE,"E2"),sQuery(id+"F0.wireOp",EDGE,"E3"),sQuery(id+"F0.wireOp",EDGE,"E4"),sQuery(id+"F0.wireOp",EDGE,"E5"),sQuery(id+"F0.wireOp",EDGE,"E6"),sQuery(id+"F0.wireOp",EDGE,"E7"),sQuery(id+"F0.wireOp",EDGE,"E8"),sQuery(id+"F0.wireOp",EDGE,"E9")])],"isStart":true}),makeQuery(id+"F10.opExtrude","SWEPT_FACE",FACE,{"disambiguationData":[OSD([sQuery(id+"F9.wireOp",EDGE,"E39.2")])]})]});
            extrude(context, id + "F23", {"entities" : qUnion([Q0]), "endBound" : BoundingType.UP_TO_SURFACE, "depth" : 25 * mm, "endBoundEntityFace" : qUnion([Q1]), "offsetDistance" : 25 * mm, "hasSecondDirection" : true, "secondDirectionBound" : SecondDirectionBoundingType.UP_TO_SURFACE, "secondDirectionOppositeDirection" : true, "secondDirectionDepth" : 25 * mm, "secondDirectionBoundEntityFace" : qUnion([Q2])});
        }
        {
            var Q0;
            Q0=qCreatedBy(makeId("Front.planeOp"),FACE);
            var sketch = newSketch(context, id + "F24", { "sketchPlane" : qUnion([Q0])});
            skLineSegment(sketch, "E111.0.0", {"start": v(496.54, -29.72) * mm, "end": v(376.66, 69.65) * mm});
            skLineSegment(sketch, "E111.0.1", {"start": v(376.66, 69.65) * mm, "end": v(-503.23, 177.69) * mm});
            skLineSegment(sketch, "E111.0.2", {"start": v(-503.23, 177.69) * mm, "end": v(-511.76, 108.2) * mm});
            skLineSegment(sketch, "E111.0.3", {"start": v(-511.76, 108.2) * mm, "end": v(366.17, 0.41) * mm});
            skLineSegment(sketch, "E111.0.4", {"start": v(366.17, 0.41) * mm, "end": v(458.25, -75.92) * mm});
            skLineSegment(sketch, "E111.0.5", {"start": v(458.25, -75.92) * mm, "end": v(496.54, -29.72) * mm});
            skSolve(sketch);
        }
        {
            var Q0;
            Q0 = qSketchRegion(id + "F24", true);
            var Q1;
            Q1=makeQuery(id+"F10.boolean.opBoolean","MERGE",FACE,{"derivedFrom":[makeQuery(id+"F1.opExtrude","CAP_FACE",FACE,{"disambiguationData":[OSD([sQuery(id+"F0.wireOp",EDGE,"E1"),sQuery(id+"F0.wireOp",EDGE,"E2"),sQuery(id+"F0.wireOp",EDGE,"E3"),sQuery(id+"F0.wireOp",EDGE,"E4"),sQuery(id+"F0.wireOp",EDGE,"E5"),sQuery(id+"F0.wireOp",EDGE,"E6"),sQuery(id+"F0.wireOp",EDGE,"E7"),sQuery(id+"F0.wireOp",EDGE,"E8"),sQuery(id+"F0.wireOp",EDGE,"E9")])],"isStart":false}),makeQuery(id+"F10.opExtrude","SWEPT_FACE",FACE,{"disambiguationData":[OSD([sQuery(id+"F9.wireOp",EDGE,"E39.0")])]})]});
            var Q2;
            Q2=makeQuery(id+"F10.boolean.opBoolean","MERGE",FACE,{"derivedFrom":[makeQuery(id+"F1.opExtrude","CAP_FACE",FACE,{"disambiguationData":[OSD([sQuery(id+"F0.wireOp",EDGE,"E1"),sQuery(id+"F0.wireOp",EDGE,"E2"),sQuery(id+"F0.wireOp",EDGE,"E3"),sQuery(id+"F0.wireOp",EDGE,"E4"),sQuery(id+"F0.wireOp",EDGE,"E5"),sQuery(id+"F0.wireOp",EDGE,"E6"),sQuery(id+"F0.wireOp",EDGE,"E7"),sQuery(id+"F0.wireOp",EDGE,"E8"),sQuery(id+"F0.wireOp",EDGE,"E9")])],"isStart":true}),makeQuery(id+"F10.opExtrude","SWEPT_FACE",FACE,{"disambiguationData":[OSD([sQuery(id+"F9.wireOp",EDGE,"E39.2")])]})]});
            extrude(context, id + "F25", {"entities" : qUnion([Q0]), "endBound" : BoundingType.UP_TO_SURFACE, "depth" : 25 * mm, "endBoundEntityFace" : qUnion([Q1]), "offsetDistance" : 25 * mm, "hasSecondDirection" : true, "secondDirectionBound" : SecondDirectionBoundingType.UP_TO_SURFACE, "secondDirectionOppositeDirection" : true, "secondDirectionDepth" : 25 * mm, "secondDirectionBoundEntityFace" : qUnion([Q2])});
        }
        {
            var Q0;
            Q0=makeQuery(id+"F1.opExtrude","SWEPT_BODY",BODY,{"disambiguationData":[OSD([sQuery(id+"F0.wireOp",EDGE,"E1"),sQuery(id+"F0.wireOp",EDGE,"E2"),sQuery(id+"F0.wireOp",EDGE,"E3"),sQuery(id+"F0.wireOp",EDGE,"E4"),sQuery(id+"F0.wireOp",EDGE,"E5"),sQuery(id+"F0.wireOp",EDGE,"E6"),sQuery(id+"F0.wireOp",EDGE,"E7"),sQuery(id+"F0.wireOp",EDGE,"E8"),sQuery(id+"F0.wireOp",EDGE,"E9")])]});
            var Q1;
            Q1=makeQuery(id+"F12.opExtrude","SWEPT_BODY",BODY,{"disambiguationData":[OSD([sQuery(id+"F11.wireOp",EDGE,"E42"),sQuery(id+"F11.wireOp",EDGE,"E43"),sQuery(id+"F11.wireOp",EDGE,"E44"),sQuery(id+"F11.wireOp",EDGE,"E45"),sQuery(id+"F11.wireOp",EDGE,"E46"),sQuery(id+"F11.wireOp",EDGE,"E47"),sQuery(id+"F11.wireOp",EDGE,"E48"),sQuery(id+"F11.wireOp",EDGE,"E49"),sQuery(id+"F11.wireOp",EDGE,"E50"),sQuery(id+"F11.wireOp",EDGE,"E51")])]});
            var Q2;
            Q2=makeQuery(id+"F21.opExtrude","SWEPT_BODY",BODY,{"disambiguationData":[OSD([sQuery(id+"F20.wireOp",EDGE,"E105.0.8"),sQuery(id+"F20.wireOp",EDGE,"E106.1.2"),sQuery(id+"F20.wireOp",EDGE,"E106.1.3"),sQuery(id+"F20.wireOp",EDGE,"E106.1.13"),sQuery(id+"F20.wireOp",EDGE,"E107.0.0"),sQuery(id+"F20.wireOp",EDGE,"E107.0.1"),sQuery(id+"F20.wireOp",EDGE,"E107.0.8"),sQuery(id+"F20.wireOp",EDGE,"E108"),sQuery(id+"F20.wireOp",EDGE,"E109")])]});
            booleanBodies(context, id + "F26", {"operationType" : BooleanOperationType.SUBTRACTION, "tools" : qUnion([Q0, Q1]), "targets" : qUnion([Q2]), "keepTools" : true});
        }
        {
            var Q0;
            Q0=makeQuery(id+"F1.opExtrude","SWEPT_BODY",BODY,{"disambiguationData":[OSD([sQuery(id+"F0.wireOp",EDGE,"E1"),sQuery(id+"F0.wireOp",EDGE,"E2"),sQuery(id+"F0.wireOp",EDGE,"E3"),sQuery(id+"F0.wireOp",EDGE,"E4"),sQuery(id+"F0.wireOp",EDGE,"E5"),sQuery(id+"F0.wireOp",EDGE,"E6"),sQuery(id+"F0.wireOp",EDGE,"E7"),sQuery(id+"F0.wireOp",EDGE,"E8"),sQuery(id+"F0.wireOp",EDGE,"E9")])]});
            var Q1;
            Q1=makeQuery(id+"F23.opExtrude","SWEPT_BODY",BODY,{"disambiguationData":[OSD([sQuery(id+"F22.wireOp",EDGE,"E110.0.0"),sQuery(id+"F22.wireOp",EDGE,"E110.0.1"),sQuery(id+"F22.wireOp",EDGE,"E110.0.2"),sQuery(id+"F22.wireOp",EDGE,"E110.0.3"),sQuery(id+"F22.wireOp",EDGE,"E110.0.4"),sQuery(id+"F22.wireOp",EDGE,"E110.0.5"),sQuery(id+"F22.wireOp",EDGE,"E110.0.6"),sQuery(id+"F22.wireOp",EDGE,"E110.0.7"),sQuery(id+"F22.wireOp",EDGE,"E110.0.8"),sQuery(id+"F22.wireOp",EDGE,"E110.0.9"),sQuery(id+"F22.wireOp",EDGE,"E110.0.10"),sQuery(id+"F22.wireOp",EDGE,"E110.0.11"),sQuery(id+"F22.wireOp",EDGE,"E110.0.12")])]});
            booleanBodies(context, id + "F27", {"operationType" : BooleanOperationType.SUBTRACTION, "tools" : qUnion([Q0]), "targets" : qUnion([Q1]), "keepTools" : true});
        }
        {
            var Q0;
            Q0=makeQuery(id+"F16.opExtrude","SWEPT_BODY",BODY,{"disambiguationData":[OSD([sQuery(id+"F15.wireOp",EDGE,"E61"),sQuery(id+"F15.wireOp",EDGE,"E62"),sQuery(id+"F15.wireOp",EDGE,"E63"),sQuery(id+"F15.wireOp",EDGE,"E64"),sQuery(id+"F15.wireOp",EDGE,"E65"),sQuery(id+"F15.wireOp",EDGE,"E67")])]});
            var Q1;
            Q1=makeQuery(id+"F1.opExtrude","SWEPT_BODY",BODY,{"disambiguationData":[OSD([sQuery(id+"F0.wireOp",EDGE,"E1"),sQuery(id+"F0.wireOp",EDGE,"E2"),sQuery(id+"F0.wireOp",EDGE,"E3"),sQuery(id+"F0.wireOp",EDGE,"E4"),sQuery(id+"F0.wireOp",EDGE,"E5"),sQuery(id+"F0.wireOp",EDGE,"E6"),sQuery(id+"F0.wireOp",EDGE,"E7"),sQuery(id+"F0.wireOp",EDGE,"E8"),sQuery(id+"F0.wireOp",EDGE,"E9")])]});
            var Q2;
            Q2=makeQuery(id+"F25.opExtrude","SWEPT_BODY",BODY,{"disambiguationData":[OSD([sQuery(id+"F24.wireOp",EDGE,"E111.0.0"),sQuery(id+"F24.wireOp",EDGE,"E111.0.1"),sQuery(id+"F24.wireOp",EDGE,"E111.0.2"),sQuery(id+"F24.wireOp",EDGE,"E111.0.3"),sQuery(id+"F24.wireOp",EDGE,"E111.0.4"),sQuery(id+"F24.wireOp",EDGE,"E111.0.5")])]});
            booleanBodies(context, id + "F28", {"operationType" : BooleanOperationType.SUBTRACTION, "tools" : qUnion([Q0, Q1]), "targets" : qUnion([Q2]), "keepTools" : true});
        }
    });
